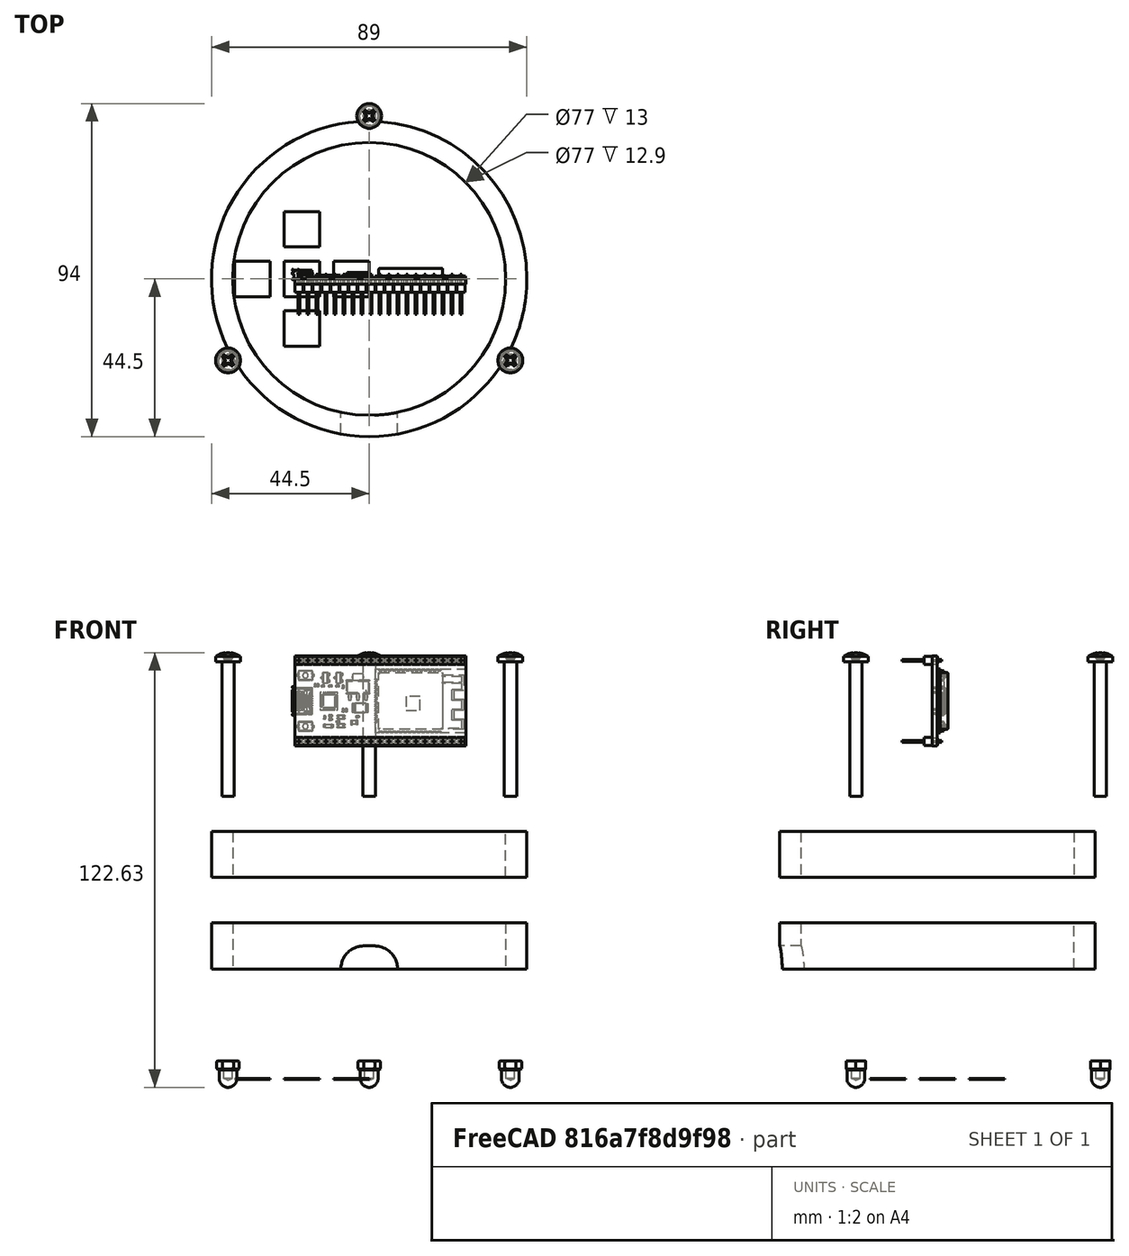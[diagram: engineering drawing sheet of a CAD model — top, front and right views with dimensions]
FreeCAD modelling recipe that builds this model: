
FCSTD DOCUMENT  (FreeCAD 2022.709R28846 (Git))
Label: infinity_02_exploded2
License: Other
LicenseURL: https://ohwr.org/project/cernohl/wikis/Documents/CERN-OHL-version-2
objects: Part::Feature×98, TechDraw::DrawViewDimension×36, TechDraw::DrawViewBalloon×17, PartDesign::ShapeBinder×12, TechDraw::DrawProjGroupItem×12, Sketcher::SketchObject×10, App::DocumentObjectGroupPython×9, PartDesign::Body×8, TechDraw::DrawSVGTemplate×8, TechDraw::DrawPage×8, TechDraw::DrawHatch×8, PartDesign::Plane×7, PartDesign::Pad×7, Part::FeaturePython×6, TechDraw::DrawProjGroup×6, Part::Part2DObjectPython×4, App::DocumentObjectGroup×3, PartDesign::Pocket×2, TechDraw::DrawViewPart×2, Spreadsheet::Sheet×1, +2 more types
note: 172 computed .brp shape members not serialized (recipe doc carries the construction recipe); baked Part::Feature solids carry a one-line shape summary decoded from their .brp

FEATURE [Spreadsheet::Sheet] Spreadsheet
  PythonMode = false
  ShowCells = 0
  TreeRank = 0
  cells = B1=Enter board size values here manually; C1=NOTES; D1=Micro_Pro; E1=Nano; F1=ESP8266 NodeMCU; G1=ESP32 NodeMCU; H1=Add more boards; I1=Add more boards; A2=Length of the microcontroller board - choose from list (and add more as required); B2(Length)==48mm; D2==34mm; E2==47mm; F2==48mm; G2==48mm; A3=Width of the microcontroller board; B3(width)==26mm; D3==21mm; E3==21mm; F3==26mm; G3==26mm; A4=Screw hole diameter; B4(screw_hole_dia)==3mm; C4=Adds 0.2mm to screw hole diameter; A5=Main Inner circumference; B5(inner_circumference)==240mm; C5=for ESP32 IoT course, make this number divisible by 12 so that 12 LEDs can be placed around circumference for a future clock; A6=Acrylic Thickness; B6(acrylic_thickness)==2.9mm; A7=LED strip width; B7(led_strip_width)==10mm; C7=use this to adjust the height of the upper spacer
FEATURE [Sketcher::SketchObject] Sketch005
  ArcFitTolerance = 0
  AttachmentSupport = -> [XY_Plane010]
  FullyConstrained = true
  MapMode = 5
  Support = -> [XY_Plane010]
  TreeRank = 0
  expr: Constraints[1] = Spreadsheet.inner_circumference / 3.14159
  sketch-geometry (53):
    g0: Circle CenterX=0 CenterY=0 CenterZ=0 NormalX=0 NormalY=0 NormalZ=1 AngleXU=0 Radius=38.1972
    g1: Circle CenterX=0 CenterY=0 CenterZ=0 NormalX=0 NormalY=0 NormalZ=1 AngleXU=0 Radius=44.5
    g2: Circle CenterX=0 CenterY=0 CenterZ=0 NormalX=0 NormalY=0 NormalZ=1 AngleXU=0 Radius=50
    g3: Circle CenterX=0 CenterY=0 CenterZ=0 NormalX=0 NormalY=0 NormalZ=1 AngleXU=0 Radius=38.5
    g4: LineSegment StartX=38.2587 StartY=9.99981 StartZ=0 EndX=28.1331 EndY=27.7894 EndZ=0
    g5: LineSegment StartX=28.1331 StartY=27.7894 StartZ=0 EndX=10.4692 EndY=38.1329 EndZ=0
    g6: LineSegment StartX=10.4692 StartY=38.1329 StartZ=0 EndX=-9.99981 EndY=38.2587 EndZ=0
    g7: LineSegment StartX=-9.99981 StartY=38.2587 StartZ=0 EndX=-27.7894 EndY=28.1331 EndZ=0
    g8: LineSegment StartX=-27.7894 StartY=28.1331 StartZ=0 EndX=-38.1329 EndY=10.4692 EndZ=0
    g9: LineSegment StartX=-38.1329 StartY=10.4692 StartZ=0 EndX=-38.2587 EndY=-9.99981 EndZ=0
    g10: LineSegment StartX=-38.2587 StartY=-9.99981 StartZ=0 EndX=-28.1331 EndY=-27.7894 EndZ=0
    g11: LineSegment StartX=-28.1331 StartY=-27.7894 StartZ=0 EndX=-10.4692 EndY=-38.1329 EndZ=0
    g12: LineSegment StartX=-10.4692 StartY=-38.1329 StartZ=0 EndX=9.99981 EndY=-38.2587 EndZ=0
    g13: LineSegment StartX=9.99981 StartY=-38.2587 StartZ=0 EndX=27.7894 EndY=-28.1331 EndZ=0
    g14: LineSegment StartX=27.7894 StartY=-28.1331 StartZ=0 EndX=38.1329 EndY=-10.4692 EndZ=0
    g15: LineSegment StartX=38.1329 StartY=-10.4692 StartZ=0 EndX=38.2587 EndY=9.99981 EndZ=0
    g16: Circle [constr] CenterX=0 CenterY=0 CenterZ=0 NormalX=0 NormalY=0 NormalZ=1 AngleXU=0 Radius=39.5439
    g17: LineSegment StartX=0 StartY=0 StartZ=0 EndX=0 EndY=38.1972 EndZ=0
    g18: LineSegment StartX=0 StartY=0 StartZ=0 EndX=19.0986 EndY=33.0798 EndZ=0
    g19: LineSegment StartX=0 StartY=0 StartZ=0 EndX=33.0798 EndY=19.0986 EndZ=0
    g20: LineSegment StartX=0 StartY=0 StartZ=0 EndX=38.1972 EndY=3.5e-15 EndZ=0
    g21: LineSegment StartX=0 StartY=0 StartZ=0 EndX=33.0798 EndY=-19.0986 EndZ=0
    g22: LineSegment StartX=0 StartY=0 StartZ=0 EndX=19.0986 EndY=-33.0798 EndZ=0
    g23: LineSegment StartX=0 StartY=0 StartZ=0 EndX=1.85e-14 EndY=-38.1972 EndZ=0
    g24: LineSegment StartX=0 StartY=0 StartZ=0 EndX=-19.0986 EndY=-33.0798 EndZ=0
    g25: LineSegment StartX=0 StartY=0 StartZ=0 EndX=-33.0798 EndY=-19.0986 EndZ=0
    g26: LineSegment StartX=0 StartY=0 StartZ=0 EndX=-38.1972 EndY=-5.03e-14 EndZ=0
    g27: LineSegment StartX=0 StartY=0 StartZ=0 EndX=-33.0798 EndY=19.0986 EndZ=0
    g28: LineSegment StartX=0 StartY=0 StartZ=0 EndX=-19.0986 EndY=33.0798 EndZ=0
    g29: LineSegment StartX=0 StartY=0 StartZ=0 EndX=3.99992 EndY=38.1726 EndZ=0
    g30: LineSegment StartX=0 StartY=0 StartZ=0 EndX=-3.99992 EndY=38.2218 EndZ=0
    g31: LineSegment StartX=0 StartY=0 StartZ=0 EndX=15.6469 EndY=35.101 EndZ=0
    g32: LineSegment StartX=0 StartY=0 StartZ=0 EndX=22.5504 EndY=31.0585 EndZ=0
    g33: LineSegment StartX=0 StartY=0 StartZ=0 EndX=31.1011 EndY=22.5749 EndZ=0
    g34: LineSegment StartX=0 StartY=0 StartZ=0 EndX=35.0584 EndY=15.6223 EndZ=0
    g35: LineSegment StartX=0 StartY=0 StartZ=0 EndX=38.2218 EndY=3.99992 EndZ=0
    g36: LineSegment StartX=0 StartY=0 StartZ=0 EndX=38.1726 EndY=-3.99992 EndZ=0
    g37: LineSegment StartX=0 StartY=0 StartZ=0 EndX=35.101 EndY=-15.6469 EndZ=0
    g38: LineSegment StartX=0 StartY=0 StartZ=0 EndX=31.0585 EndY=-22.5504 EndZ=0
    g39: LineSegment StartX=0 StartY=0 StartZ=0 EndX=22.5749 EndY=-31.1011 EndZ=0
    g40: LineSegment StartX=0 StartY=0 StartZ=0 EndX=15.6223 EndY=-35.0584 EndZ=0
    g41: LineSegment StartX=0 StartY=0 StartZ=0 EndX=3.99992 EndY=-38.2218 EndZ=0
    g42: LineSegment StartX=0 StartY=0 StartZ=0 EndX=-3.99992 EndY=-38.1726 EndZ=0
    g43: LineSegment StartX=0 StartY=0 StartZ=0 EndX=-15.6469 EndY=-35.101 EndZ=0
    g44: LineSegment StartX=0 StartY=0 StartZ=0 EndX=-22.5504 EndY=-31.0585 EndZ=0
    g45: LineSegment StartX=0 StartY=0 StartZ=0 EndX=-31.1011 EndY=-22.5749 EndZ=0
    g46: LineSegment StartX=0 StartY=0 StartZ=0 EndX=-35.0584 EndY=-15.6223 EndZ=0
    g47: LineSegment StartX=0 StartY=0 StartZ=0 EndX=-38.2218 EndY=-3.99992 EndZ=0
    g48: LineSegment StartX=0 StartY=0 StartZ=0 EndX=-38.1726 EndY=3.99992 EndZ=0
    g49: LineSegment StartX=0 StartY=0 StartZ=0 EndX=-35.101 EndY=15.6469 EndZ=0
    g50: LineSegment StartX=0 StartY=0 StartZ=0 EndX=-31.0585 EndY=22.5504 EndZ=0
    g51: LineSegment StartX=0 StartY=0 StartZ=0 EndX=-22.5749 EndY=31.1011 EndZ=0
    g52: LineSegment StartX=0 StartY=0 StartZ=0 EndX=-15.6223 EndY=35.0584 EndZ=0
  constraints (143):
    c: Coincident(g0,g-1)
    c: Diameter(g0) = 76.3944
    c: Coincident(g1,g0)
    c: Diameter(g1) = 89
    c: Coincident(g2,g0)
    c: Diameter(g2) = 100
    c: Coincident(g3,g0)
    c: Diameter(g3) = 77
    c: Coincident(g4,g5)
    c: Coincident(g5,g6)
    c: Coincident(g6,g7)
    c: Coincident(g7,g8)
    c: Coincident(g8,g9)
    c: Coincident(g9,g10)
    c: Coincident(g10,g11)
    c: Coincident(g11,g12)
    c: Coincident(g12,g13)
    c: Coincident(g13,g14)
    c: Coincident(g14,g15)
    c: Coincident(g15,g4)
    c: Equal(g4, g5-g15) x11
    c: PointOnObject(g4,g16)
    c: PointOnObject(g5,g16)
    c: PointOnObject(g6,g16)
    c: PointOnObject(g7,g16)
    c: PointOnObject(g8,g16)
    c: PointOnObject(g9,g16)
    c: PointOnObject(g10,g16)
    c: PointOnObject(g11,g16)
    c: PointOnObject(g12,g16)
    c: PointOnObject(g13,g16)
    c: PointOnObject(g14,g16)
    c: Coincident(g16,g0)
    c: Coincident(g17,g0)
    c: PointOnObject(g17,g6)
    c: Distance(g17,g6) = 10
    c: Coincident(g18,g0)
    c: PointOnObject(g18,g5)
    c: Coincident(g19,g0)
    c: PointOnObject(g19,g4)
    c: Coincident(g20,g0)
    c: PointOnObject(g20,g15)
    c: Coincident(g21,g0)
    c: PointOnObject(g21,g14)
    c: Coincident(g22,g0)
    c: PointOnObject(g22,g13)
    c: Coincident(g23,g0)
    c: PointOnObject(g23,g12)
    c: Coincident(g24,g0)
    c: PointOnObject(g24,g11)
    c: Coincident(g25,g0)
    c: PointOnObject(g25,g10)
    c: Coincident(g26,g0)
    c: PointOnObject(g26,g9)
    c: Coincident(g27,g0)
    c: PointOnObject(g27,g8)
    c: Coincident(g28,g0)
    c: PointOnObject(g28,g7)
    c: Angle(g18,g17) = 0.523599
    c: Angle(g19,g18) = 0.523599
    c: Angle(g20,g19) = 0.523599
    c: Angle(g21,g20) = 0.523599
    c: Angle(g22,g21) = 0.523599
    c: Angle(g23,g22) = 0.523599
    c: Angle(g24,g23) = 0.523599
    c: Angle(g25,g24) = 0.523599
    c: Angle(g26,g25) = 0.523599
    c: Angle(g27,g26) = 0.523599
    c: Angle(g28,g27) = 0.523599
    c: PointOnObject(g4,g16)
    c: Vertical(g17)
    c: PointOnObject(g17,g0)
    c: Coincident(g29,g0)
    c: PointOnObject(g29,g6)
    c: Coincident(g30,g0)
    c: Symmetric(g30,g29,g17)
    c: Distance(g29,g30) = 8
    c: Coincident(g31,g0)
    c: PointOnObject(g31,g5)
    c: Coincident(g32,g0)
    c: PointOnObject(g32,g5)
    c: Angle(g31,g30) = 0.523599
    c: Angle(g32,g29) = 0.523599
    c: Coincident(g33,g0)
    c: PointOnObject(g33,g4)
    c: Coincident(g34,g0)
    c: PointOnObject(g34,g4)
    c: Angle(g33,g31) = 0.523599
    c: Angle(g34,g32) = 0.523599
    c: Coincident(g35,g0)
    c: PointOnObject(g35,g15)
    c: Coincident(g36,g0)
    c: PointOnObject(g36,g15)
    c: Angle(g35,g33) = 0.523599
    c: Angle(g36,g34) = 0.523599
    c: Coincident(g37,g0)
    c: PointOnObject(g37,g14)
    c: Coincident(g38,g0)
    c: PointOnObject(g38,g14)
    c: Angle(g37,g35) = 0.523599
    c: Angle(g38,g36) = 0.523599
    c: Coincident(g39,g0)
    c: PointOnObject(g39,g13)
    c: Coincident(g40,g0)
    c: PointOnObject(g40,g13)
    c: Angle(g39,g37) = 0.523599
    c: Angle(g40,g38) = 0.523599
    c: Coincident(g41,g0)
    c: PointOnObject(g41,g12)
    c: Coincident(g42,g0)
    c: PointOnObject(g42,g12)
    c: Angle(g41,g39) = 0.523599
    c: Angle(g42,g40) = 0.523599
    c: Coincident(g43,g0)
    c: PointOnObject(g43,g11)
    c: Coincident(g44,g0)
    c: PointOnObject(g44,g11)
    c: Angle(g43,g41) = 0.523599
    c: Angle(g44,g42) = 0.523599
    c: Coincident(g45,g0)
    c: PointOnObject(g45,g10)
    c: Coincident(g46,g0)
    c: PointOnObject(g46,g10)
    c: Angle(g45,g43) = 0.523599
    c: Angle(g46,g44) = 0.523599
    c: Coincident(g47,g0)
    c: PointOnObject(g47,g9)
    c: Coincident(g48,g0)
    c: PointOnObject(g48,g9)
    c: Angle(g47,g45) = 0.523599
    c: Angle(g48,g46) = 0.523599
    c: Coincident(g49,g0)
    c: PointOnObject(g49,g8)
    c: Coincident(g50,g0)
    c: PointOnObject(g50,g8)
    c: Angle(g49,g47) = 0.523599
    c: Angle(g50,g48) = 0.523599
    c: Coincident(g51,g0)
    c: PointOnObject(g51,g7)
    c: Coincident(g52,g0)
    c: PointOnObject(g52,g7)
    c: Angle(g51,g49) = 0.523599
    c: Angle(g52,g50) = 0.523599
FEATURE [PartDesign::Body] Body010
  AutoGroupSolids = false
  ClaimAllChildren = false
  ExportMode = 0
  Group = -> [Sketch005]
  Origin = -> Origin013
  TreeRank = 0
  _ExportChildren = -> [Sketch005]
  _GroupVersion = 1
FEATURE [PartDesign::ShapeBinder] ShapeBinder
  Support = -> [Sketch005]
  TraceSupport = false
  TreeRank = 0
FEATURE [PartDesign::Plane] DatumPlane
  AttachmentSupport = -> [ShapeBinder]
  Length = 10
  MapMode = 11
  MinimumLength = 10
  MinimumWidth = 10
  Placement = pos=(0,0,0) rot=(0,0,1;1.5708rad)
  ResizeMode = 0
  Support = -> [ShapeBinder]
  TreeRank = 0
  Width = 10
FEATURE [Sketcher::SketchObject] Sketch
  ArcFitTolerance = 0
  AttachmentSupport = -> [DatumPlane]
  ExternalGeometry = -> [ShapeBinder]
  FullyConstrained = true
  MapMode = 5
  Placement = pos=(0,0,0) rot=(0,0,1;1.5708rad)
  Support = -> [DatumPlane]
  TreeRank = 0
  sketch-geometry (2):
    g0: Circle CenterX=0 CenterY=0 CenterZ=0 NormalX=0 NormalY=0 NormalZ=1 AngleXU=0 Radius=44.5
    g1: Circle CenterX=0 CenterY=0 CenterZ=0 NormalX=0 NormalY=0 NormalZ=1 AngleXU=0 Radius=38.5
  constraints (4):
    c: Coincident(g0,g-4)
    c: Coincident(g1,g0)
    c: Equal(g1,g-4)
    c: Equal(g-3,g0)
FEATURE [PartDesign::Pad] Pad
  ClaimChildren = false
  Direction = (1,1,1)
  Fit = 0
  FitJoin = 0
  InnerFit = 0
  InnerFitJoin = 0
  InnerTaperAngle = 0
  InnerTaperAngleRev = 0
  Length = 5
  Length2 = 8
  NewSolid = false
  Placement = pos=(0,0,0) rot=(0,0,1;1.5708rad)
  Profile = -> Sketch
  Reversed = true
  Suppress = false
  TreeRank = 0
  Type = 4
  _ProfileBasedVersion = 0
FEATURE [PartDesign::Plane] DatumPlane002
  AttachmentOffset = pos=(0,0,0) rot=(1,0,0;1.5708rad)
  AttachmentSupport = -> [Pad]
  Length = 89
  MapMode = 45
  MinimumLength = 10
  MinimumWidth = 10
  Placement = pos=(3e-16,-1.42e-14,-1.5) rot=(1,0,0;1.5708rad)
  ResizeMode = 0
  Support = -> [Pad]
  TreeRank = 0
  Width = 13
FEATURE [Sketcher::SketchObject] Sketch007
  ArcFitTolerance = 0
  AttachmentSupport = -> [DatumPlane002]
  ExternalGeometry = -> [Pad]
  FullyConstrained = true
  MapMode = 5
  Placement = pos=(3e-16,-1.42e-14,-1.5) rot=(1,0,0;1.5708rad)
  Support = -> [DatumPlane002]
  TreeRank = 0
  sketch-geometry (4):
    g0: ArcOfCircle CenterX=-1.5 CenterY=-6.5 CenterZ=0 NormalX=0 NormalY=0 NormalZ=1 AngleXU=0 Radius=6.5 StartAngle=1.5708 EndAngle=4.71239
    g1: ArcOfCircle CenterX=1.5 CenterY=-6.5 CenterZ=0 NormalX=0 NormalY=0 NormalZ=1 AngleXU=0 Radius=6.5 StartAngle=4.71239 EndAngle=7.85398
    g2: LineSegment StartX=-1.5 StartY=-13 StartZ=0 EndX=1.5 EndY=-13 EndZ=0
    g3: LineSegment StartX=-1.5 StartY=9e-16 StartZ=0 EndX=1.5 EndY=1.8e-15 EndZ=0
  constraints (9):
    c: Tangent(g0,g3) = 1.5708
    c: Tangent(g0,g2) = -1.5708
    c: Tangent(g2,g1) = -1.5708
    c: Tangent(g3,g1) = 1.5708
    c: Horizontal(g2)
    c: DistanceX(g0,g1) = 3
    c: Symmetric(g1,g0,g-2)
    c: Radius(g0) = 6.5
    c: PointOnObject(g0,g-3)
FEATURE [PartDesign::Pocket] Pocket
  BaseFeature = -> Pad
  ClaimChildren = false
  Fit = 0
  FitJoin = 0
  InnerFit = 0
  InnerFitJoin = 0
  InnerTaperAngle = 0
  InnerTaperAngleRev = 0
  Length = 26
  Length2 = 100
  NewSolid = false
  Placement = pos=(0,0,0) rot=(0,0,1;1.5708rad)
  Profile = -> Sketch007
  Reversed = true
  Suppress = false
  TreeRank = 0
  Type = 1
  _ProfileBasedVersion = 0
FEATURE [PartDesign::Body] Body  label="PCB_lower_spacer"
  AutoGroupSolids = false
  ClaimAllChildren = false
  ExportMode = 0
  Group = -> [ShapeBinder,DatumPlane,Sketch,Pad,DatumPlane002,Sketch007,Pocket]
  Origin = -> Origin
  Placement = pos=(0,0,-67) rot=(0,0,1;0rad)
  Tip = -> Pocket
  TreeRank = 0
  _ExportChildren = -> [ShapeBinder,DatumPlane,Pad,DatumPlane002,Pocket]
  _GroupVersion = 1
FEATURE [PartDesign::ShapeBinder] ShapeBinder002
  Support = -> [Sketch005]
  TraceSupport = false
  TreeRank = 0
FEATURE [PartDesign::ShapeBinder] ShapeBinder003
  Placement = pos=(0,0,-67) rot=(0,0,1;0rad)
  Support = -> [Body]
  TraceSupport = false
  TreeRank = 0
FEATURE [PartDesign::Plane] DatumPlane004
  AttachmentSupport = -> [ShapeBinder003]
  Length = 100
  MapMode = 5
  MinimumLength = 10
  MinimumWidth = 10
  Placement = pos=(0,0,-62) rot=(0,0,1;0rad)
  ResizeMode = 0
  Support = -> [ShapeBinder003]
  TreeRank = 0
  Width = 99.9333
FEATURE [Sketcher::SketchObject] Sketch009
  ArcFitTolerance = 0
  AttachmentSupport = -> [DatumPlane004]
  ExternalGeometry = -> [ShapeBinder002]
  FullyConstrained = true
  MapMode = 5
  Placement = pos=(0,0,-62) rot=(0,0,1;0rad)
  Support = -> [DatumPlane004]
  TreeRank = 0
  expr: Constraints[1] = Spreadsheet.screw_hole_dia
  sketch-geometry (8):
    g0: Circle CenterX=0 CenterY=0 CenterZ=0 NormalX=0 NormalY=0 NormalZ=1 AngleXU=0 Radius=50
    g1: Circle CenterX=0 CenterY=46 CenterZ=0 NormalX=0 NormalY=0 NormalZ=1 AngleXU=0 Radius=1.5
    g2: Circle CenterX=-39.8372 CenterY=-23 CenterZ=0 NormalX=0 NormalY=0 NormalZ=1 AngleXU=0 Radius=1.5
    g3: Circle CenterX=39.8372 CenterY=-23 CenterZ=0 NormalX=0 NormalY=0 NormalZ=1 AngleXU=0 Radius=1.5
    g4: LineSegment [constr] StartX=0 StartY=46 StartZ=0 EndX=-39.8372 EndY=-23 EndZ=0
    g5: LineSegment [constr] StartX=-39.8372 StartY=-23 StartZ=0 EndX=39.8372 EndY=-23 EndZ=0
    g6: LineSegment [constr] StartX=39.8372 StartY=-23 StartZ=0 EndX=0 EndY=46 EndZ=0
    g7: Circle [constr] CenterX=0 CenterY=0 CenterZ=0 NormalX=0 NormalY=0 NormalZ=1 AngleXU=0 Radius=46
  constraints (19):
    c: Equal(g-3,g0)
    c: Diameter(g1) = 3
    c: Equal(g1,g2)
    c: Equal(g1,g3)
    c: PointOnObject(g1,g-2)
    c: Tangent(g1,g-5)
    c: Tangent(g2,g-5)
    c: Tangent(g3,g-5)
    c: Coincident(g4,g5)
    c: Coincident(g5,g6)
    c: Coincident(g6,g4)
    c: Equal(g4,g5)
    c: Equal(g4,g6)
    c: PointOnObject(g4,g7)
    c: Coincident(g6,g1)
    c: Coincident(g2,g4)
    c: Coincident(g3,g5)
    c: Coincident(g0,g-5)
    c: Coincident(g7,g0)
FEATURE [PartDesign::Pad] Pad002
  ClaimChildren = false
  Direction = (1,1,1)
  Fit = 0
  FitJoin = 0
  InnerFit = 0
  InnerFitJoin = 0
  InnerTaperAngle = 0
  InnerTaperAngleRev = 0
  Length = 2.9
  Length2 = 100
  NewSolid = false
  Placement = pos=(0,0,-62) rot=(0,0,1;0rad)
  Profile = -> Sketch009
  Suppress = false
  TreeRank = 0
  Type = 0
  _ProfileBasedVersion = 0
  expr: Length = Spreadsheet.acrylic_thickness
FEATURE [Part::Feature] Solid089
  TreeRank = 0
  shape: bbox 0.66 x 0.051 x 0.304 mm, 6 faces (baked)
FEATURE [Part::Feature] Solid090
  TreeRank = 0
  shape: bbox 0.5016 x 0.5016 x 1 mm, 66 faces (baked)
FEATURE [Part::Feature] Solid091
  TreeRank = 0
  shape: bbox 0.66 x 0.051 x 0.304 mm, 6 faces (baked)
FEATURE [Part::Feature] Solid092
  TreeRank = 0
  shape: bbox 0.66 x 0.051 x 0.304 mm, 6 faces (baked)
FEATURE [Part::Feature] Solid093
  TreeRank = 0
  shape: bbox 1.02 x 0.52 x 0.52 mm, 15 faces (baked)
FEATURE [Part::Feature] Solid094
  TreeRank = 0
  shape: bbox 0.65 x 1.325 x 2.3 mm, 11 faces (baked)
FEATURE [Part::Feature] Solid095
  TreeRank = 0
  shape: bbox 2.126 x 0.2178 x 1.073 mm, 52 faces (baked)
FEATURE [Part::Feature] Solid096
  TreeRank = 0
  shape: bbox 0.4 x 0.2 x 0.8 mm, 8 faces (baked)
FEATURE [Part::Feature] Solid097
  TreeRank = 0
  shape: bbox 4.2 x 1.55 x 0.3 mm, 15 faces (baked)
FEATURE [Part::Feature] Solid098
  TreeRank = 0
  shape: bbox 1.624 x 0.5 x 1.624 mm, 6 faces (baked)
FEATURE [Part::Feature] Solid099
  TreeRank = 0
  shape: bbox 1.02 x 0.52 x 0.52 mm, 15 faces (baked)
FEATURE [Part::Feature] Solid100
  TreeRank = 0
  shape: bbox 1 x 0.5016 x 0.5016 mm, 66 faces (baked)
FEATURE [Part::Feature] Solid101
  TreeRank = 0
  shape: bbox 3.9 x 1.7 x 2.5 mm, 6 faces (baked)
FEATURE [Part::Feature] Solid102
  TreeRank = 0
  shape: bbox 0.4 x 0.2 x 0.8 mm, 8 faces (baked)
FEATURE [Part::Feature] Solid103
  TreeRank = 0
  shape: bbox 4.2 x 1.55 x 0.3 mm, 15 faces (baked)
FEATURE [Part::Feature] Solid104
  TreeRank = 0
  shape: bbox 4.2 x 1.55 x 0.3 mm, 15 faces (baked)
FEATURE [Part::Feature] Solid105
  TreeRank = 0
  shape: bbox 1 x 0.5016 x 0.5016 mm, 66 faces (baked)
FEATURE [Part::Feature] Solid106
  TreeRank = 0
  shape: bbox 6.707 x 1.804 x 3.709 mm, 14 faces (baked)
FEATURE [Part::Feature] Solid107
  TreeRank = 0
  shape: bbox 0.52 x 0.52 x 1.02 mm, 15 faces (baked)
FEATURE [Part::Feature] Solid108
  TreeRank = 0
  shape: bbox 2 x 0.8516 x 1.252 mm, 66 faces (baked)
FEATURE [Part::Feature] Solid109
  TreeRank = 0
  shape: bbox 1.624 x 0.5 x 1.624 mm, 6 faces (baked)
FEATURE [Part::Feature] Solid110
  TreeRank = 0
  shape: bbox 3.9 x 1.2 x 0.1 mm, 14 faces (baked)
FEATURE [Part::Feature] Solid111
  TreeRank = 0
  shape: bbox 0.8392 x 0.9032 x 1.792 mm, 14 faces (baked)
FEATURE [Part::Feature] Solid112
  TreeRank = 0
  shape: bbox 3.9 x 1.7 x 2.5 mm, 6 faces (baked)
FEATURE [Part::Feature] Solid113
  TreeRank = 0
  shape: bbox 2.5 x 1.11 x 3 mm, 49 faces (baked)
FEATURE [Part::Feature] Solid114
  TreeRank = 0
  shape: bbox 0.304 x 0.051 x 0.66 mm, 6 faces (baked)
FEATURE [Part::Feature] Solid115
  TreeRank = 0
  shape: bbox 1.333 x 0.3705 x 1.073 mm, 18 faces (baked)
FEATURE [Part::Feature] Solid116 .. Solid121  x6 (patterned run collapsed; names and placements below)
  TreeRank = 0
  shape: bbox 0.304 x 0.051 x 0.66 mm, 6 faces (baked)
FEATURE [Part::Feature] Solid122
  TreeRank = 0
  shape: bbox 0.66 x 0.051 x 0.304 mm, 6 faces (baked)
FEATURE [Part::Feature] Solid123
  TreeRank = 0
  shape: bbox 0.52 x 0.52 x 1.02 mm, 15 faces (baked)
FEATURE [Part::Feature] Solid124
  TreeRank = 0
  shape: bbox 0.66 x 0.051 x 0.304 mm, 6 faces (baked)
FEATURE [Part::Feature] Solid125
  TreeRank = 0
  shape: bbox 3.9 x 1.2 x 0.1 mm, 14 faces (baked)
FEATURE [Part::Feature] Solid126 .. Solid130  x5 (patterned run collapsed; names and placements below)
  TreeRank = 0
  shape: bbox 0.66 x 0.051 x 0.304 mm, 6 faces (baked)
FEATURE [Part::Feature] Solid131
  TreeRank = 0
  shape: bbox 4.16 x 2.41 x 6.91 mm, 176 faces (baked)
FEATURE [Part::Feature] Solid132
  TreeRank = 0
  shape: bbox 0.304 x 0.051 x 0.66 mm, 6 faces (baked)
FEATURE [Part::Feature] Solid133
  TreeRank = 0
  shape: bbox 0.4 x 0.2 x 0.8 mm, 8 faces (baked)
FEATURE [Part::Feature] Solid134 .. Solid138  x5 (patterned run collapsed; names and placements below)
  TreeRank = 0
  shape: bbox 0.304 x 0.051 x 0.66 mm, 6 faces (baked)
FEATURE [Part::Feature] Solid139
  TreeRank = 0
  shape: bbox 0.52 x 0.52 x 1.02 mm, 15 faces (baked)
FEATURE [Part::Feature] Solid140
  TreeRank = 0
  shape: bbox 0.304 x 0.051 x 0.66 mm, 6 faces (baked)
FEATURE [Part::Feature] Solid141
  TreeRank = 0
  shape: bbox 3.352 x 0.051 x 3.352 mm, 6 faces (baked)
FEATURE [Part::Feature] Solid142
  TreeRank = 0
  shape: bbox 1.65 x 1.05 x 1.05 mm, 14 faces (baked)
FEATURE [Part::Feature] Solid143
  TreeRank = 0
  shape: bbox 0.4875 x 0.5625 x 0.9375 mm, 11 faces (baked)
FEATURE [Part::Feature] Solid144
  TreeRank = 0
  shape: bbox 0.4 x 0.2 x 0.8 mm, 8 faces (baked)
FEATURE [Part::Feature] Solid145
  TreeRank = 0
  shape: bbox 1.333 x 0.3705 x 1.073 mm, 18 faces (baked)
FEATURE [Part::Feature] Solid146
  TreeRank = 0
  shape: bbox 0.4875 x 0.5625 x 0.9375 mm, 11 faces (baked)
FEATURE [Part::Feature] Solid147
  TreeRank = 0
  shape: bbox 1 x 0.5016 x 0.5016 mm, 66 faces (baked)
FEATURE [Part::Feature] Solid148
  TreeRank = 0
  shape: bbox 0.8392 x 0.9032 x 1.792 mm, 14 faces (baked)
FEATURE [Part::Feature] Solid149
  TreeRank = 0
  shape: bbox 1.02 x 0.52 x 0.52 mm, 15 faces (baked)
FEATURE [Part::Feature] Solid150
  TreeRank = 0
  shape: bbox 3.151 x 0.9032 x 1.792 mm, 14 faces (baked)
FEATURE [Part::Feature] Solid151
  TreeRank = 0
  shape: bbox 3.3 x 1.775 x 2.7 mm, 7 faces (baked)
FEATURE [Part::Feature] Solid152
  TreeRank = 0
  shape: bbox 0.65 x 1.325 x 2.3 mm, 11 faces (baked)
FEATURE [Part::Feature] Solid153
  TreeRank = 0
  shape: bbox 48.28 x 11.27 x 25.42 mm, 1344 faces (baked)
FEATURE [Part::Feature] Solid154
  TreeRank = 0
  shape: bbox 0.1854 x 0.003 x 0.1854 mm, 4 faces (baked)
FEATURE [Part::Feature] Solid155
  TreeRank = 0
  shape: bbox 2.126 x 0.2178 x 1.073 mm, 52 faces (baked)
FEATURE [Part::Feature] Solid156
  TreeRank = 0
  shape: bbox 4.2 x 1.55 x 0.3 mm, 15 faces (baked)
FEATURE [Part::Feature] Solid157
  TreeRank = 0
  shape: bbox 3.9 x 0.1 x 2.5 mm, 30 faces (baked)
FEATURE [Part::Feature] Solid158
  TreeRank = 0
  shape: bbox 0.52 x 0.52 x 1.02 mm, 15 faces (baked)
FEATURE [Part::Feature] Solid159
  TreeRank = 0
  shape: bbox 0.1 x 0.6 x 0.8 mm, 6 faces (baked)
FEATURE [Part::Feature] Solid160
  TreeRank = 0
  shape: bbox 2.5 x 1.11 x 3 mm, 49 faces (baked)
FEATURE [Part::Feature] Solid161
  TreeRank = 0
  shape: bbox 0.1 x 0.6 x 0.8 mm, 6 faces (baked)
FEATURE [Part::Feature] Solid162
  TreeRank = 0
  shape: bbox 3.9 x 1.2 x 0.1 mm, 14 faces (baked)
FEATURE [Part::Feature] Solid163
  TreeRank = 0
  shape: bbox 1.02 x 0.52 x 0.52 mm, 15 faces (baked)
FEATURE [Part::Feature] Solid164
  TreeRank = 0
  shape: bbox 5.63 x 3.797 x 8.183 mm, 257 faces (baked)
FEATURE [Part::Feature] Solid165
  TreeRank = 0
  shape: bbox 3.9 x 0.1 x 2.5 mm, 30 faces (baked)
FEATURE [Part::Feature] Solid166
  TreeRank = 0
  shape: bbox 4.2 x 1.55 x 0.3 mm, 15 faces (baked)
FEATURE [Part::Feature] Solid167
  TreeRank = 0
  shape: bbox 0.1 x 0.6 x 0.8 mm, 6 faces (baked)
FEATURE [Part::Feature] Solid168
  TreeRank = 0
  shape: bbox 0.1 x 0.6 x 0.8 mm, 6 faces (baked)
FEATURE [Part::Feature] Solid169
  TreeRank = 0
  shape: bbox 3.9 x 1.2 x 0.1 mm, 14 faces (baked)
FEATURE [Part::Feature] Solid170
  TreeRank = 0
  shape: bbox 0.52 x 0.52 x 1.02 mm, 15 faces (baked)
FEATURE [Part::Feature] Solid171
  TreeRank = 0
  shape: bbox 0.8392 x 0.9032 x 1.792 mm, 14 faces (baked)
FEATURE [Part::Feature] Solid172
  TreeRank = 0
  shape: bbox 0.2502 x 0.002 x 0.2502 mm, 4 faces (baked)
FEATURE [Part::Feature] Solid173
  TreeRank = 0
  shape: bbox 5.004 x 0.94 x 5.004 mm, 6 faces (baked)
FEATURE [Part::Feature] Solid174
  TreeRank = 0
  shape: bbox 0.66 x 0.051 x 0.304 mm, 6 faces (baked)
FEATURE [Part::Feature] Solid175
  TreeRank = 0
  shape: bbox 25.54 x 3.035 x 18.07 mm, 584 faces (baked)
FEATURE [Part::Feature] Solid176
  TreeRank = 0
  shape: bbox 0.66 x 0.051 x 0.304 mm, 6 faces (baked)
FEATURE [Part::Feature] Solid177
  TreeRank = 0
  shape: bbox 0.66 x 0.051 x 0.304 mm, 6 faces (baked)
FEATURE [Part::Feature] Solid178
  TreeRank = 0
  shape: bbox 0.66 x 0.051 x 0.304 mm, 6 faces (baked)
FEATURE [Part::Compound2] Compound001  label="ESP32Wroom4"
  Links = -> [Solid089,Solid090,Solid091,Solid092,Solid093,Solid094,Solid095,Solid096,Solid097,Solid098,Solid099,Solid100,Solid101,Solid102,Solid103,Solid104,Solid105,Solid106,Solid107,Solid108,Solid109,Solid110,Solid111,Solid112,Solid113,Solid114,Solid115,Solid116,Solid117,Solid118,Solid119,Solid120,Solid121,Solid122,Solid123,Solid124,Solid125,Solid126,Solid127,Solid128,Solid129,Solid130,Solid131,Solid132,+46 more]
  Placement = pos=(0.5,-15,-90) rot=(-0.57735,-0.57735,0.57735;2.0944rad)
  TreeRank = 0
FEATURE [Sketcher::SketchObject] Sketch010
  ArcFitTolerance = 0
  AttachmentSupport = -> [Pad002]
  ExternalGeometry = -> [ShapeBinder002]
  FullyConstrained = true
  MapMode = 5
  Placement = pos=(0,0,-59.1) rot=(0,0,1;0rad)
  Support = -> [Pad002]
  TreeRank = 0
  sketch-geometry (5):
    g0: ArcOfCircle CenterX=-4 CenterY=-34.5 CenterZ=0 NormalX=0 NormalY=0 NormalZ=1 AngleXU=0 Radius=2 StartAngle=1.5708 EndAngle=4.71239
    g1: ArcOfCircle CenterX=4 CenterY=-34.5 CenterZ=0 NormalX=0 NormalY=0 NormalZ=1 AngleXU=0 Radius=2 StartAngle=4.71239 EndAngle=7.85398
    g2: LineSegment StartX=-4 StartY=-36.5 StartZ=0 EndX=4 EndY=-36.5 EndZ=0
    g3: LineSegment StartX=-4 StartY=-32.5 StartZ=0 EndX=4 EndY=-32.5 EndZ=0
    g4: LineSegment [constr] StartX=0 StartY=-38.5 StartZ=0 EndX=0 EndY=-36.5 EndZ=0
  constraints (13):
    c: Tangent(g0,g3) = 1.5708
    c: Tangent(g0,g2) = -1.5708
    c: Tangent(g2,g1) = -1.5708
    c: Tangent(g3,g1) = 1.5708
    c: Horizontal(g2)
    c: Diameter(g0) = 4
    c: Symmetric(g0,g1,g-2)
    c: DistanceX(g0,g1) = 8
    c: PointOnObject(g4,g-3)
    c: PointOnObject(g4,g2)
    c: Vertical(g4)
    c: PointOnObject(g4,g-2)
    c: DistanceY(g4,g4) = 2
FEATURE [PartDesign::Pocket] Pocket001
  BaseFeature = -> Pad002
  ClaimChildren = false
  Fit = 0
  FitJoin = 0
  InnerFit = 0
  InnerFitJoin = 0
  InnerTaperAngle = 0
  InnerTaperAngleRev = 0
  Length = 5
  Length2 = 100
  NewSolid = false
  Placement = pos=(0,0,-62) rot=(0,0,1;0rad)
  Profile = -> Sketch010
  Suppress = false
  TreeRank = 0
  Type = 1
  _ProfileBasedVersion = 0
FEATURE [PartDesign::Body] Body012  label="Mirror"
  AutoGroupSolids = false
  ClaimAllChildren = false
  ExportMode = 0
  Group = -> [ShapeBinder002,ShapeBinder003,DatumPlane004,Sketch009,Pad002,Sketch010,Pocket001]
  Origin = -> Origin015
  Placement = pos=(0,0,5) rot=(0,0,1;0rad)
  Tip = -> Pocket001
  TreeRank = 0
  _ExportChildren = -> [ShapeBinder002,ShapeBinder003,DatumPlane004,Pad002,Pocket001]
  _GroupVersion = 1
FEATURE [PartDesign::ShapeBinder] ShapeBinder004 .. ShapeBinder007  x4 (patterned run collapsed; names and placements below)
  Support = -> [Sketch005]
  TraceSupport = false
  TreeRank = 0
FEATURE [PartDesign::Plane] DatumPlane008
  AttachmentSupport = -> [Pocket]
  Length = 98.9466
  MapMode = 5
  MinimumLength = 10
  MinimumWidth = 10
  Placement = pos=(0,0,-8) rot=(0.707107,0.707107,0;3.14159rad)
  ResizeMode = 0
  Support = -> [Pocket]
  TreeRank = 0
  Width = 99.95
FEATURE [Sketcher::SketchObject] Sketch014
  ArcFitTolerance = 0
  AttachmentSupport = -> [DatumPlane008]
  ExternalGeometry = -> [ShapeBinder007]
  FullyConstrained = true
  MapMode = 5
  Placement = pos=(0,0,-8) rot=(0.707107,0.707107,0;3.14159rad)
  Support = -> [DatumPlane008]
  TreeRank = 0
  expr: Constraints[2] = Spreadsheet.screw_hole_dia
  sketch-geometry (62):
    g0: ArcOfCircle CenterX=-7e-16 CenterY=7e-16 CenterZ=0 NormalX=0 NormalY=0 NormalZ=1 AngleXU=0 Radius=50 StartAngle=3.35146 EndAngle=9.21491
    g1: Circle CenterX=-23 CenterY=-39.8372 CenterZ=0 NormalX=0 NormalY=0 NormalZ=1 AngleXU=0 Radius=1.5
    g2: Circle CenterX=46 CenterY=0 CenterZ=0 NormalX=0 NormalY=0 NormalZ=1 AngleXU=0 Radius=1.5
    g3: Circle CenterX=-23 CenterY=39.8372 CenterZ=0 NormalX=0 NormalY=0 NormalZ=1 AngleXU=0 Radius=1.5
    g4: LineSegment [constr] StartX=-23 StartY=-39.8372 StartZ=0 EndX=46 EndY=0 EndZ=0
    g5: LineSegment [constr] StartX=46 StartY=0 StartZ=0 EndX=-23 EndY=39.8372 EndZ=0
    g6: LineSegment [constr] StartX=-23 StartY=39.8372 StartZ=0 EndX=-23 EndY=-39.8372 EndZ=0
    g7: Circle [constr] CenterX=-7e-16 CenterY=7e-16 CenterZ=0 NormalX=0 NormalY=0 NormalZ=1 AngleXU=0 Radius=46
    g8: ArcOfCircle CenterX=22 CenterY=0 CenterZ=0 NormalX=0 NormalY=0 NormalZ=1 AngleXU=0 Radius=6 StartAngle=0.523599 EndAngle=5.75959
    g9: ArcOfCircle CenterX=34 CenterY=0 CenterZ=0 NormalX=0 NormalY=0 NormalZ=1 AngleXU=0 Radius=2 StartAngle=4.71239 EndAngle=7.85398
    g10: LineSegment StartX=28.9282 StartY=-2 StartZ=0 EndX=34 EndY=-2 EndZ=0
    g11: LineSegment StartX=28.9282 StartY=2 StartZ=0 EndX=34 EndY=2 EndZ=0
    g12: ArcOfCircle CenterX=28.9282 CenterY=4 CenterZ=0 NormalX=0 NormalY=0 NormalZ=1 AngleXU=0 Radius=2 StartAngle=3.66519 EndAngle=4.71239
    g13: ArcOfCircle CenterX=28.9282 CenterY=-4 CenterZ=0 NormalX=0 NormalY=0 NormalZ=1 AngleXU=0 Radius=2 StartAngle=1.5708 EndAngle=2.61799
    g14: LineSegment [constr] StartX=-5 StartY=7e-16 StartZ=0 EndX=5 EndY=7e-16 EndZ=0
    g15: LineSegment [constr] StartX=5 StartY=7e-16 StartZ=0 EndX=5 EndY=-10 EndZ=0
    g16: LineSegment [constr] StartX=5 StartY=-10 StartZ=0 EndX=-5 EndY=-10 EndZ=0
    g17: LineSegment [constr] StartX=-5 StartY=-10 StartZ=0 EndX=-5 EndY=0 EndZ=0
    g18: LineSegment [constr] StartX=-19 StartY=-14 StartZ=0 EndX=-9 EndY=-14 EndZ=0
    g19: LineSegment [constr] StartX=-9 StartY=-14 StartZ=0 EndX=-9 EndY=-24 EndZ=0
    g20: LineSegment [constr] StartX=-9 StartY=-24 StartZ=0 EndX=-19 EndY=-24 EndZ=0
    g21: LineSegment [constr] StartX=-19 StartY=-24 StartZ=0 EndX=-19 EndY=-14 EndZ=0
    g22: LineSegment [constr] StartX=9 StartY=-14 StartZ=0 EndX=19 EndY=-14 EndZ=0
    g23: LineSegment [constr] StartX=19 StartY=-14 StartZ=0 EndX=19 EndY=-24 EndZ=0
    g24: LineSegment [constr] StartX=19 StartY=-24 StartZ=0 EndX=9 EndY=-24 EndZ=0
    g25: LineSegment [constr] StartX=9 StartY=-24 StartZ=0 EndX=9 EndY=-14 EndZ=0
    g26: LineSegment [constr] StartX=-5 StartY=-14 StartZ=0 EndX=5 EndY=-14 EndZ=0
    g27: LineSegment [constr] StartX=5 StartY=-14 StartZ=0 EndX=5 EndY=-24 EndZ=0
    g28: LineSegment [constr] StartX=5 StartY=-24 StartZ=0 EndX=-5 EndY=-24 EndZ=0
    g29: LineSegment [constr] StartX=-5 StartY=-24 StartZ=0 EndX=-5 EndY=-14 EndZ=0
    g30: LineSegment [constr] StartX=-5 StartY=-28 StartZ=0 EndX=5 EndY=-28 EndZ=0
    g31: LineSegment [constr] StartX=5 StartY=-28 StartZ=0 EndX=5 EndY=-38 EndZ=0
    g32: LineSegment [constr] StartX=5 StartY=-38 StartZ=0 EndX=-5 EndY=-38 EndZ=0
    g33: LineSegment [constr] StartX=-5 StartY=-38 StartZ=0 EndX=-5 EndY=-28 EndZ=0
    g34: LineSegment [constr] StartX=-5 StartY=-10 StartZ=0 EndX=-5 EndY=-14 EndZ=0
    g35: LineSegment [constr] StartX=-5 StartY=-14 StartZ=0 EndX=-9 EndY=-14 EndZ=0
    g36: LineSegment [constr] StartX=5 StartY=-10 StartZ=0 EndX=5 EndY=-14 EndZ=0
    g37: LineSegment [constr] StartX=5 StartY=-14 StartZ=0 EndX=9 EndY=-14 EndZ=0
    g38: LineSegment [constr] StartX=5 StartY=-28 StartZ=0 EndX=5 EndY=-24 EndZ=0
    g39: LineSegment [constr] StartX=5 StartY=-24 StartZ=0 EndX=9 EndY=-24 EndZ=0
    g40: LineSegment [constr] StartX=-5 StartY=-28 StartZ=0 EndX=-5 EndY=-24 EndZ=0
    g41: LineSegment [constr] StartX=-5 StartY=-24 StartZ=0 EndX=-9 EndY=-24 EndZ=0
    g42: LineSegment [constr] StartX=-7 StartY=-12 StartZ=0 EndX=7 EndY=-12 EndZ=0
    g43: LineSegment [constr] StartX=7 StartY=-12 StartZ=0 EndX=7 EndY=-26 EndZ=0
    g44: LineSegment [constr] StartX=7 StartY=-26 StartZ=0 EndX=-7 EndY=-26 EndZ=0
    g45: LineSegment [constr] StartX=-7 StartY=-26 StartZ=0 EndX=-7 EndY=-12 EndZ=0
    g46: LineSegment [constr] StartX=-1.3e-15 StartY=-12 StartZ=0 EndX=-1.3e-15 EndY=-26 EndZ=0
    g47: LineSegment [constr] StartX=7 StartY=-19 StartZ=0 EndX=-7 EndY=-19 EndZ=0
    g48: Circle CenterX=-7 CenterY=-12 CenterZ=0 NormalX=0 NormalY=0 NormalZ=1 AngleXU=0 Radius=1.5
    g49: Circle CenterX=-1.3e-15 CenterY=-12 CenterZ=0 NormalX=0 NormalY=0 NormalZ=1 AngleXU=0 Radius=1.5
    g50: Circle CenterX=7 CenterY=-12 CenterZ=0 NormalX=0 NormalY=0 NormalZ=1 AngleXU=0 Radius=1.5
    g51: Circle CenterX=7 CenterY=-19 CenterZ=0 NormalX=0 NormalY=0 NormalZ=1 AngleXU=0 Radius=1.5
    g52: Circle CenterX=7 CenterY=-26 CenterZ=0 NormalX=0 NormalY=0 NormalZ=1 AngleXU=0 Radius=1.5
    g53: Circle CenterX=-1.3e-15 CenterY=-26 CenterZ=0 NormalX=0 NormalY=0 NormalZ=1 AngleXU=0 Radius=1.5
    g54: Circle CenterX=-7 CenterY=-26 CenterZ=0 NormalX=0 NormalY=0 NormalZ=1 AngleXU=0 Radius=1.5
    g55: Circle CenterX=-7 CenterY=-19 CenterZ=0 NormalX=0 NormalY=0 NormalZ=1 AngleXU=0 Radius=1.5
    g56: ArcOfCircle CenterX=-36.9468 CenterY=1e-16 CenterZ=0 NormalX=0 NormalY=0 NormalZ=1 AngleXU=0 Radius=8 StartAngle=4.71239 EndAngle=7.85398
    g57: LineSegment StartX=-36.9468 StartY=8 StartZ=0 EndX=-46.9468 EndY=8 EndZ=0
    g58: LineSegment StartX=-36.9468 StartY=-8 StartZ=0 EndX=-46.9468 EndY=-8 EndZ=0
    g59: ArcOfCircle CenterX=-46.9468 CenterY=-10 CenterZ=0 NormalX=0 NormalY=0 NormalZ=1 AngleXU=0 Radius=2 StartAngle=1.5708 EndAngle=3.35146
    g60: ArcOfCircle CenterX=-46.9468 CenterY=10 CenterZ=0 NormalX=0 NormalY=0 NormalZ=1 AngleXU=0 Radius=2 StartAngle=2.93172 EndAngle=4.71239
    g61: LineSegment [constr] StartX=34 StartY=0 StartZ=0 EndX=46 EndY=0 EndZ=0
  constraints (155):
    c: Coincident(g0,g-3)
    c: Equal(g0,g-3)
    c: Diameter(g3) = 3
    c: Equal(g3,g2)
    c: Equal(g3,g1)
    c: Tangent(g1,g-4)
    c: Coincident(g4,g5)
    c: Coincident(g5,g6)
    c: Coincident(g6,g4)
    c: Equal(g4,g5)
    c: Equal(g4,g6)
    c: PointOnObject(g5,g7)
    c: Coincident(g6,g1)
    c: Coincident(g2,g4)
    c: Coincident(g3,g5)
    c: Coincident(g7,g0)
    c: Tangent(g10,g9) = -1.5708
    c: Tangent(g11,g9) = 1.5708
    c: Diameter(g9) = 4
    c: Diameter(g8) = 12
    c: Tangent(g8,g12) = 1.5708
    c: Tangent(g11,g12) = -1.5708
    c: Tangent(g8,g13) = 1.5708
    c: Tangent(g10,g13) = 1.5708
    c: Radius(g13) = 2
    c: Equal(g13,g12)
    c: Coincident(g14,g15)
    c: Coincident(g15,g16)
    c: Coincident(g16,g17)
    c: Coincident(g17,g14)
    c: Horizontal(g14)
    c: Horizontal(g16)
    c: Vertical(g15)
    c: Vertical(g17)
    c: Coincident(g18,g19)
    c: Coincident(g19,g20)
    c: Coincident(g20,g21)
    c: Coincident(g21,g18)
    c: Horizontal(g18)
    c: Horizontal(g20)
    c: Vertical(g19)
    c: Vertical(g21)
    c: Coincident(g22,g23)
    c: Coincident(g23,g24)
    c: Coincident(g24,g25)
    c: Coincident(g25,g22)
    c: Horizontal(g22)
    c: Horizontal(g24)
    c: Vertical(g23)
    c: Vertical(g25)
    c: Coincident(g26,g27)
    c: Coincident(g27,g28)
    c: Coincident(g28,g29)
    c: Coincident(g29,g26)
    c: Horizontal(g26)
    c: Horizontal(g28)
    c: Vertical(g27)
    c: Vertical(g29)
    c: Coincident(g30,g31)
    c: Coincident(g31,g32)
    c: Coincident(g32,g33)
    c: Coincident(g33,g30)
    c: Horizontal(g30)
    c: Horizontal(g32)
    c: Vertical(g31)
    c: Vertical(g33)
    c: Equal(g16,g15)
    c: Equal(g19,g20)
    c: Equal(g31,g32)
    c: Equal(g24,g23)
    c: Equal(g27,g28)
    c: Equal(g14,g18)
    c: Equal(g18,g30)
    c: Equal(g30,g22)
    c: Equal(g22,g26)
    c: DistanceX(g14,g14) = 10
    c: Vertical(g16,g26)
    c: Vertical(g28,g30)
    c: Horizontal(g26,g18)
    c: Horizontal(g26,g22)
    c: Coincident(g34,g16)
    c: Coincident(g34,g26)
    c: Coincident(g35,g26)
    c: Coincident(g35,g18)
    c: Coincident(g36,g15)
    c: Coincident(g36,g26)
    c: Coincident(g37,g26)
    c: Coincident(g37,g22)
    c: Coincident(g38,g30)
    c: Coincident(g38,g27)
    c: Coincident(g39,g27)
    c: Coincident(g39,g24)
    c: Coincident(g40,g30)
    c: Coincident(g40,g28)
    c: Coincident(g41,g28)
    c: Coincident(g41,g19)
    c: Equal(g34,g40)
    c: Equal(g35,g37)
    c: Equal(g35,g34)
    c: DistanceX(g35,g35) = 4
    c: Tangent(g2,g-4)
    c: Coincident(g42,g43)
    c: Coincident(g43,g44)
    c: Coincident(g44,g45)
    c: Coincident(g45,g42)
    c: Symmetric(g18,g26,g45)
    c: Symmetric(g26,g22,g43)
    c: Symmetric(g15,g26,g42)
    c: Symmetric(g27,g30,g44)
    c: PointOnObject(g46,g44)
    c: Vertical(g46)
    c: PointOnObject(g47,g45)
    c: Horizontal(g47)
    c: Symmetric(g42,g42,g46)
    c: Symmetric(g42,g43,g47)
    c: Coincident(g48,g42)
    c: Coincident(g49,g46)
    c: Coincident(g50,g42)
    c: Coincident(g51,g47)
    c: Coincident(g52,g43)
    c: Coincident(g53,g46)
    c: Coincident(g54,g44)
    c: Coincident(g55,g47)
    c: Equal(g54,g55)
    c: Equal(g55,g48)
    c: Equal(g48,g49)
    c: Equal(g49,g50)
    c: Equal(g50,g52)
    c: Equal(g52,g53)
    c: Equal(g53,g51)
    c: Diameter(g51) = 3
    c: Tangent(g56,g58) = 1.5708
    c: Tangent(g56,g57) = -1.5708
    c: Diameter(g56) = 16
    c: Tangent(g58,g59) = -1.5708
    c: Tangent(g0,g59) = -1.5708
    c: Tangent(g57,g60) = 1.5708
    c: Tangent(g0,g60) = -1.5708
    c: Radius(g60) = 2
    c: Equal(g60,g59)
    c: Tangent(g3,g-4)
    c: Equal(g11,g10)
    c: Parallel(g10,g11)
    c: Horizontal(g8,g9)
    c: Distance(g8,g9) = 12
    c: Coincident(g61,g9)
    c: PointOnObject(g61,g7)
    c: Horizontal(g61)
    c: Distance(g61) = 12
    c: PointOnObject(g9,g-1)
    c: Symmetric(g14,g14,g0)
    c: Parallel(g57,g58)
    c: Symmetric(g56,g56,g-1)
    c: DistanceX(g57,g57) = 10
    c: Horizontal(g9,g2)
FEATURE [PartDesign::Pad] Pad006
  ClaimChildren = false
  Direction = (1,1,1)
  Fit = 0
  FitJoin = 0
  InnerFit = 0
  InnerFitJoin = 0
  InnerTaperAngle = 0
  InnerTaperAngleRev = 0
  Length = 2.9
  Length2 = 100
  NewSolid = false
  Placement = pos=(0,0,-8) rot=(0.707107,0.707107,0;3.14159rad)
  Profile = -> Sketch014
  Suppress = false
  TreeRank = 0
  Type = 0
  _ProfileBasedVersion = 0
  expr: Length = Spreadsheet.acrylic_thickness
FEATURE [Part::FeaturePython] Screw  label="(M3.5)x38-Screw"  # Fasteners workbench fastener (typed FeaturePython)
  Placement = pos=(-39.8372,-23,11.7) rot=(0,0,1;0rad)
  TreeRank = 0
  baseObject = -> Body015 [Edge12]
  diameter = 5
  invert = false
  leftHanded = false
  length = 11
  lengthCustom = 38
  matchOuter = false
  offset = 0
  thread = false
  type = 40
FEATURE [Part::FeaturePython] Screw001  label="(M3.5)x38-Screw309"  # Fasteners workbench fastener (typed FeaturePython)
  Placement = pos=(39.8372,-23,11.7) rot=(0,0,1;0rad)
  TreeRank = 0
  baseObject = -> Body015 [Edge9]
  diameter = 5
  invert = false
  leftHanded = false
  length = 11
  lengthCustom = 38
  matchOuter = false
  offset = 0
  thread = false
  type = 40
FEATURE [Part::FeaturePython] Screw002  label="(M3.5)x38-Screw310"  # Fasteners workbench fastener (typed FeaturePython)
  Placement = pos=(0,46,11.7) rot=(0,0,1;0rad)
  TreeRank = 0
  baseObject = -> Body015 [Edge15]
  diameter = 5
  invert = false
  leftHanded = false
  length = 11
  lengthCustom = 38
  matchOuter = false
  offset = 0
  thread = false
  type = 40
FEATURE [Part::FeaturePython] Nut  label="M3-Nut"  # Fasteners workbench fastener (typed FeaturePython)
  Placement = pos=(-39.8372,-23,-100.9) rot=(-1,0,0;3.14159rad)
  TreeRank = 0
  baseObject = -> Body016 [Edge69]
  diameter = 1
  invert = false
  leftHanded = false
  matchOuter = false
  offset = 0
  thread = false
  type = 9
FEATURE [Part::FeaturePython] Nut001  label="M3-Nut447"  # Fasteners workbench fastener (typed FeaturePython)
  Placement = pos=(39.8372,-23,-100.9) rot=(-1,0,0;3.14159rad)
  TreeRank = 0
  baseObject = -> Body016 [Edge63]
  diameter = 1
  invert = false
  leftHanded = false
  matchOuter = false
  offset = 0
  thread = false
  type = 9
FEATURE [Part::FeaturePython] Nut002  label="M3-Nut448"  # Fasteners workbench fastener (typed FeaturePython)
  Placement = pos=(1e-14,46,-100.9) rot=(-1,0,0;3.14159rad)
  TreeRank = 0
  baseObject = -> Body016 [Edge66]
  diameter = 1
  invert = false
  leftHanded = false
  matchOuter = false
  offset = 0
  thread = false
  type = 9
FEATURE [PartDesign::ShapeBinder] ShapeBinder008
  Placement = pos=(0,0,5) rot=(0,0,1;0rad)
  Support = -> [Body012]
  TraceSupport = false
  TreeRank = 5
FEATURE [PartDesign::Plane] DatumPlane005
  AttachmentSupport = -> [ShapeBinder008]
  Length = 89
  MapMode = 5
  MinimumLength = 10
  MinimumWidth = 10
  Placement = pos=(0,0,-54.1) rot=(0,0,1;0rad)
  ResizeMode = 0
  Support = -> [ShapeBinder008]
  TreeRank = 0
  Width = 89
FEATURE [Sketcher::SketchObject] Sketch011
  ArcFitTolerance = 0
  AttachmentSupport = -> [DatumPlane005]
  ExternalGeometry = -> [ShapeBinder004]
  FullyConstrained = true
  MapMode = 5
  Placement = pos=(0,0,-54.1) rot=(0,0,1;0rad)
  Support = -> [DatumPlane005]
  TreeRank = 0
  sketch-geometry (2):
    g0: Circle CenterX=0 CenterY=0 CenterZ=0 NormalX=0 NormalY=0 NormalZ=1 AngleXU=0 Radius=44.5
    g1: Circle CenterX=0 CenterY=0 CenterZ=0 NormalX=0 NormalY=0 NormalZ=1 AngleXU=0 Radius=38.5
  constraints (4):
    c: Coincident(g0,g-4)
    c: Coincident(g1,g0)
    c: Equal(g1,g-4)
    c: Equal(g-3,g0)
FEATURE [PartDesign::Pad] Pad003
  ClaimChildren = false
  Direction = (1,1,1)
  Fit = 0
  FitJoin = 0
  InnerFit = 0
  InnerFitJoin = 0
  InnerTaperAngle = 0
  InnerTaperAngleRev = 0
  Length = 12.9
  Length2 = 100
  NewSolid = false
  Placement = pos=(0,0,-54.1) rot=(0,0,1;0rad)
  Profile = -> Sketch011
  Suppress = false
  TreeRank = 0
  Type = 0
  _ProfileBasedVersion = 0
  expr: Length = Spreadsheet.led_strip_width + Spreadsheet.acrylic_thickness
FEATURE [PartDesign::Body] Body013  label="Upper_spacer"
  AutoGroupSolids = false
  ClaimAllChildren = false
  ExportMode = 0
  Group = -> [ShapeBinder004,DatumPlane005,Sketch011,Pad003,ShapeBinder008]
  Origin = -> Origin016
  Placement = pos=(0,0,5) rot=(0,0,1;0rad)
  Tip = -> Pad003
  TreeRank = 0
  _ExportChildren = -> [ShapeBinder004,DatumPlane005,Pad003,ShapeBinder008]
  _GroupVersion = 1
FEATURE [PartDesign::ShapeBinder] ShapeBinder009
  Placement = pos=(0,0,5) rot=(0,0,1;0rad)
  Support = -> [Body013]
  TraceSupport = false
  TreeRank = 6
FEATURE [PartDesign::Plane] DatumPlane006
  AttachmentSupport = -> [ShapeBinder009]
  Length = 77.4
  MapMode = 5
  MinimumLength = 10
  MinimumWidth = 10
  Placement = pos=(0,0,-36.2) rot=(0,0,1;0rad)
  ResizeMode = 0
  Support = -> [ShapeBinder009]
  TreeRank = 0
  Width = 77.3484
FEATURE [Sketcher::SketchObject] Sketch012
  ArcFitTolerance = 0
  AttachmentSupport = -> [DatumPlane006]
  ExternalGeometry = -> [ShapeBinder005]
  FullyConstrained = true
  MapMode = 5
  Placement = pos=(0,0,-36.2) rot=(0,0,1;0rad)
  Support = -> [DatumPlane006]
  TreeRank = 0
  sketch-geometry (2):
    g0: Circle CenterX=0 CenterY=0 CenterZ=0 NormalX=0 NormalY=0 NormalZ=1 AngleXU=0 Radius=38.7
    g1: LineSegment [constr] StartX=-38.7 StartY=0 StartZ=0 EndX=-38.5 EndY=0 EndZ=0
  constraints (6):
    c: Coincident(g0,g-3)
    c: PointOnObject(g1,g0)
    c: PointOnObject(g1,g-3)
    c: Horizontal(g1)
    c: PointOnObject(g1,g-1)
    c: DistanceX(g1,g1) = 0.2
FEATURE [PartDesign::Pad] Pad004
  ClaimChildren = false
  Direction = (1,1,1)
  Fit = 0
  FitJoin = 0
  InnerFit = 0
  InnerFitJoin = 0
  InnerTaperAngle = 0
  InnerTaperAngleRev = 0
  Length = 2.9
  Length2 = 100
  NewSolid = false
  Placement = pos=(0,0,-36.2) rot=(0,0,1;0rad)
  Profile = -> Sketch012
  Reversed = true
  Suppress = false
  TreeRank = 0
  Type = 0
  _ProfileBasedVersion = 0
  expr: Length = Spreadsheet.acrylic_thickness
FEATURE [PartDesign::Body] Body014  label="Mirror_one_way"
  AutoGroupSolids = false
  ClaimAllChildren = false
  ExportMode = 0
  Group = -> [ShapeBinder005,DatumPlane006,Sketch012,Pad004,ShapeBinder009]
  Origin = -> Origin017
  Placement = pos=(0,0,5) rot=(0,0,1;0rad)
  Tip = -> Pad004
  TreeRank = 0
  _ExportChildren = -> [ShapeBinder005,DatumPlane006,Pad004,ShapeBinder009]
  _GroupVersion = 1
FEATURE [PartDesign::ShapeBinder] ShapeBinder010
  Placement = pos=(0,0,5) rot=(0,0,1;0rad)
  Support = -> [Body013]
  TraceSupport = false
  TreeRank = 7
FEATURE [PartDesign::Plane] DatumPlane007
  AttachmentSupport = -> [ShapeBinder010]
  Length = 100
  MapMode = 5
  MinimumLength = 10
  MinimumWidth = 10
  Placement = pos=(0,0,-36.2) rot=(0,0,1;0rad)
  ResizeMode = 0
  Support = -> [ShapeBinder010]
  TreeRank = 0
  Width = 99.9333
FEATURE [Sketcher::SketchObject] Sketch013
  ArcFitTolerance = 0
  AttachmentSupport = -> [DatumPlane007]
  ExternalGeometry = -> [ShapeBinder006]
  FullyConstrained = true
  MapMode = 5
  Placement = pos=(0,0,-36.2) rot=(0,0,1;0rad)
  Support = -> [DatumPlane007]
  TreeRank = 0
  expr: Constraints[8] = Spreadsheet.screw_hole_dia
  sketch-geometry (10):
    g0: Circle CenterX=0 CenterY=0 CenterZ=0 NormalX=0 NormalY=0 NormalZ=1 AngleXU=0 Radius=50
    g1: Circle CenterX=0 CenterY=0 CenterZ=0 NormalX=0 NormalY=0 NormalZ=1 AngleXU=0 Radius=37
    g2: LineSegment [constr] StartX=-37 StartY=0 StartZ=0 EndX=-38.5 EndY=0 EndZ=0
    g3: Circle CenterX=0 CenterY=46 CenterZ=0 NormalX=0 NormalY=0 NormalZ=1 AngleXU=0 Radius=1.5
    g4: Circle CenterX=-39.8372 CenterY=-23 CenterZ=0 NormalX=0 NormalY=0 NormalZ=1 AngleXU=0 Radius=1.5
    g5: Circle CenterX=39.8372 CenterY=-23 CenterZ=0 NormalX=0 NormalY=0 NormalZ=1 AngleXU=0 Radius=1.5
    g6: LineSegment [constr] StartX=0 StartY=46 StartZ=0 EndX=-39.8372 EndY=-23 EndZ=0
    g7: LineSegment [constr] StartX=-39.8372 StartY=-23 StartZ=0 EndX=39.8372 EndY=-23 EndZ=0
    g8: LineSegment [constr] StartX=39.8372 StartY=-23 StartZ=0 EndX=0 EndY=46 EndZ=0
    g9: Circle [constr] CenterX=0 CenterY=0 CenterZ=0 NormalX=0 NormalY=0 NormalZ=1 AngleXU=0 Radius=46
  constraints (25):
    c: Coincident(g0,g-4)
    c: Coincident(g1,g0)
    c: Equal(g-3,g0)
    c: PointOnObject(g2,g1)
    c: PointOnObject(g2,g-4)
    c: Horizontal(g2)
    c: PointOnObject(g2,g-1)
    c: DistanceX(g2,g2) = 1.5
    c: Diameter(g4) = 3
    c: Equal(g4,g5)
    c: Equal(g4,g3)
    c: PointOnObject(g3,g-2)
    c: Tangent(g3,g-5)
    c: Coincident(g6,g7)
    c: Coincident(g7,g8)
    c: Coincident(g8,g6)
    c: Equal(g6,g7)
    c: Equal(g6,g8)
    c: PointOnObject(g6,g9)
    c: PointOnObject(g7,g9)
    c: PointOnObject(g8,g9)
    c: Coincident(g9,g0)
    c: Coincident(g8,g3)
    c: Coincident(g4,g6)
    c: Coincident(g5,g7)
FEATURE [PartDesign::Pad] Pad005
  ClaimChildren = false
  Direction = (1,1,1)
  Fit = 0
  FitJoin = 0
  InnerFit = 0
  InnerFitJoin = 0
  InnerTaperAngle = 0
  InnerTaperAngleRev = 0
  Length = 2.9
  Length2 = 100
  NewSolid = false
  Placement = pos=(0,0,-36.2) rot=(0,0,1;0rad)
  Profile = -> Sketch013
  Suppress = false
  TreeRank = 0
  Type = 0
  _ProfileBasedVersion = 0
  expr: Length = Spreadsheet.acrylic_thickness
FEATURE [PartDesign::Body] Body015  label="Front_bezel"
  AutoGroupSolids = false
  ClaimAllChildren = false
  ExportMode = 0
  Group = -> [ShapeBinder006,DatumPlane007,Sketch013,Pad005,ShapeBinder010]
  Origin = -> Origin018
  Placement = pos=(0,0,45) rot=(0,0,1;0rad)
  Tip = -> Pad005
  TreeRank = 0
  _ExportChildren = -> [ShapeBinder006,DatumPlane007,Pad005,ShapeBinder010]
  _GroupVersion = 1
FEATURE [PartDesign::ShapeBinder] ShapeBinder011
  Placement = pos=(0,0,-67) rot=(0,0,1;0rad)
  Support = -> [Body]
  TraceSupport = false
  TreeRank = 8
FEATURE [PartDesign::Body] Body016  label="Back_cover"
  AutoGroupSolids = false
  ClaimAllChildren = false
  ExportMode = 0
  Group = -> [ShapeBinder007,DatumPlane008,Sketch014,Pad006,ShapeBinder011]
  Origin = -> Origin019
  Placement = pos=(0,0,-90) rot=(0,0,1;0rad)
  Tip = -> Pad006
  TreeRank = 0
  _ExportChildren = -> [ShapeBinder007,DatumPlane008,Pad006,ShapeBinder011]
  _GroupVersion = 1
FEATURE [Part::Part2DObjectPython] Shape2DView  label="Back_cover_DXF"  # Draft 2D object (typed FeaturePython)
  Base = -> Body016
  FuseArch = false
  HiddenLines = false
  InPlace = true
  Projection = (0,0,1)
  ProjectionMode = 0
  SegmentLength = 0.05
  Tessellation = false
  TreeRank = 9
  VisibleOnly = false
FEATURE [Part::Part2DObjectPython] Shape2DView001  label="Front_bezel_DXF"  # Draft 2D object (typed FeaturePython)
  Base = -> Body015
  FuseArch = false
  HiddenLines = false
  InPlace = true
  Projection = (0,0,1)
  ProjectionMode = 0
  SegmentLength = 0.05
  Tessellation = false
  TreeRank = 10
  VisibleOnly = false
FEATURE [Part::Part2DObjectPython] Shape2DView002  label="Mirror_one_way_DXF"  # Draft 2D object (typed FeaturePython)
  Base = -> Body014
  FuseArch = false
  HiddenLines = false
  InPlace = true
  Projection = (0,0,1)
  ProjectionMode = 0
  SegmentLength = 0.05
  Tessellation = false
  TreeRank = 11
  VisibleOnly = false
FEATURE [Part::Part2DObjectPython] Shape2DView003  label="Mirror_DXF"  # Draft 2D object (typed FeaturePython)
  Base = -> Body012
  FuseArch = false
  HiddenLines = false
  InPlace = true
  Projection = (0,0,1)
  ProjectionMode = 0
  SegmentLength = 0.05
  Tessellation = false
  TreeRank = 12
  VisibleOnly = false
FEATURE [App::DocumentObjectGroup] Group  label="DXF"
  ClaimAllChildren = true
  ExportMode = 1
  Group = -> [Shape2DView,Shape2DView001,Shape2DView002,Shape2DView003]
  TreeRank = 0
  _GroupVersion = 1
FEATURE [TechDraw::DrawSVGTemplate] Template
  EditableTexts = AUTHOR_NAME=Anool J M,DRAWING_TITLE=Lower Spacer,FC-DATE=02/04/2023,FC-REV=REV A,FC-SC=1:1,FC-SH=1 / 8,FC-SI=A4,FREECAD_DRAWING=77 mm ID, 89 mm OD,+3 more (map truncated)
  Height = 210
  Orientation = 1
  TreeRank = 14
  Width = 297
FEATURE [TechDraw::DrawSVGTemplate] Template001
  EditableTexts = AUTHOR_NAME=Anool J M,DRAWING_TITLE=Upper Spacer,FC-DATE=02/04/2023,FC-REV=REV A,FC-SC=1:1,FC-SH=2 / 8,FC-SI=A4,FREECAD_DRAWING=77 mm ID, 89 mm OD,+3 more (map truncated)
  Height = 210
  Orientation = 1
  TreeRank = 21
  Width = 297
FEATURE [TechDraw::DrawProjGroupItem] ProjItem002  label="Front001"
  CoarseView = false
  Direction = (0,0,1)
  Focus = 100
  HardHidden = true
  IsoCount = 0
  IsoHidden = false
  IsoVisible = false
  LockPosition = true
  Perspective = false
  Rotation = 0
  RotationVector = (1,0,0)
  ScaleType = 2
  SeamHidden = false
  SeamVisible = false
  SmoothHidden = false
  SmoothVisible = true
  Source = -> [Body013]
  TreeRank = 24
  Type = 0
  X = 0
  XDirection = (1,0,0)
  Y = 0
FEATURE [TechDraw::DrawProjGroupItem] ProjItem003  label="Bottom001"
  CoarseView = false
  Direction = (0,-1,0)
  Focus = 100
  HardHidden = true
  IsoCount = 0
  IsoHidden = false
  IsoVisible = false
  LockPosition = false
  Perspective = false
  Rotation = 0
  RotationVector = (1,0,0)
  ScaleType = 2
  SeamHidden = false
  SeamVisible = false
  SmoothHidden = false
  SmoothVisible = true
  Source = -> [Body013]
  TreeRank = 26
  Type = 5
  X = 0
  XDirection = (1,0,0)
  Y = 65.95
FEATURE [TechDraw::DrawProjGroup] ProjGroup001
  Anchor = -> ProjItem002
  AutoDistribute = true
  LockPosition = false
  ProjectionType = 0
  Rotation = 0
  ScaleType = 0
  Source = -> [Body013]
  TreeRank = 25
  Views = -> [ProjItem002,ProjItem003]
  X = 152.158
  Y = 100.518
  spacingX = 15
  spacingY = 15
FEATURE [TechDraw::DrawSVGTemplate] Template002
  EditableTexts = AUTHOR_NAME=Anool J M,DRAWING_TITLE=Mirror, 100%,FC-DATE=02/04/2023,FC-REV=REV A,FC-SC=1:1,FC-SH=3 / 8,FC-SI=A4,FREECAD_DRAWING=100 mm OD,+3 more (map truncated)
  Height = 210
  Orientation = 1
  TreeRank = 28
  Width = 297
FEATURE [TechDraw::DrawProjGroupItem] ProjItem004  label="Front002"
  CoarseView = false
  Direction = (0,0,1)
  Focus = 100
  HardHidden = true
  IsoCount = 0
  IsoHidden = false
  IsoVisible = false
  LockPosition = true
  Perspective = false
  Rotation = 0
  RotationVector = (1,0,0)
  ScaleType = 2
  SeamHidden = false
  SeamVisible = false
  SmoothHidden = false
  SmoothVisible = true
  Source = -> [Body012]
  TreeRank = 31
  Type = 0
  X = 0
  XDirection = (1,0,0)
  Y = 0
FEATURE [TechDraw::DrawProjGroupItem] ProjItem005  label="Right"
  CoarseView = false
  Direction = (1,0,1e-16)
  Focus = 100
  HardHidden = true
  IsoCount = 0
  IsoHidden = false
  IsoVisible = false
  LockPosition = false
  Perspective = false
  Rotation = 0
  RotationVector = (1,0,0)
  ScaleType = 2
  SeamHidden = false
  SeamVisible = false
  SmoothHidden = false
  SmoothVisible = true
  Source = -> [Body012]
  TreeRank = 33
  Type = 2
  X = -66.45
  XDirection = (1e-16,0,-1)
  Y = 0
FEATURE [TechDraw::DrawProjGroup] ProjGroup002
  Anchor = -> ProjItem004
  AutoDistribute = true
  LockPosition = false
  ProjectionType = 0
  Rotation = 0
  ScaleType = 0
  Source = -> [Body012]
  TreeRank = 32
  Views = -> [ProjItem004,ProjItem005]
  X = 103.115
  Y = 122.909
  spacingX = 15
  spacingY = 15
FEATURE [TechDraw::DrawSVGTemplate] Template003
  EditableTexts = AUTHOR_NAME=Anool J M,DRAWING_TITLE=Mirror, one way,FC-DATE=02/04/2023,FC-REV=REV A,FC-SC=1:1,FC-SH=4 / 8,FC-SI=A4,FREECAD_DRAWING=77.4 mm dia,+3 more (map truncated)
  Height = 210
  Orientation = 1
  TreeRank = 35
  Width = 297
FEATURE [TechDraw::DrawProjGroupItem] ProjItem006  label="Front003"
  CoarseView = false
  Direction = (0,0,1)
  Focus = 100
  HardHidden = true
  IsoCount = 0
  IsoHidden = false
  IsoVisible = false
  LockPosition = true
  Perspective = false
  Rotation = 0
  RotationVector = (1,0,0)
  ScaleType = 2
  SeamHidden = false
  SeamVisible = false
  SmoothHidden = false
  SmoothVisible = true
  Source = -> [Body014]
  TreeRank = 38
  Type = 0
  X = 0
  XDirection = (1,0,0)
  Y = 0
FEATURE [TechDraw::DrawProjGroupItem] ProjItem007  label="Right001"
  CoarseView = false
  Direction = (1,0,1e-16)
  Focus = 100
  HardHidden = true
  IsoCount = 0
  IsoHidden = false
  IsoVisible = false
  LockPosition = false
  Perspective = false
  Rotation = 0
  RotationVector = (1,0,0)
  ScaleType = 2
  SeamHidden = false
  SeamVisible = false
  SmoothHidden = false
  SmoothVisible = true
  Source = -> [Body014]
  TreeRank = 40
  Type = 2
  X = -55.15
  XDirection = (1e-16,0,-1)
  Y = 0
FEATURE [TechDraw::DrawProjGroup] ProjGroup003
  Anchor = -> ProjItem006
  AutoDistribute = true
  LockPosition = false
  ProjectionType = 0
  Rotation = 0
  ScaleType = 0
  Source = -> [Body014]
  TreeRank = 39
  Views = -> [ProjItem006,ProjItem007]
  X = 96.828
  Y = 129.074
  spacingX = 15
  spacingY = 15
FEATURE [TechDraw::DrawSVGTemplate] Template004
  EditableTexts = AUTHOR_NAME=Anool J M,DRAWING_TITLE=Front bezel,FC-DATE=02/04/2023,FC-REV=REV A,FC-SC=1:1,FC-SH=5 / 8,FC-SI=A4,FREECAD_DRAWING=100 mm OD, 74 mm ID,+3 more (map truncated)
  Height = 210
  Orientation = 1
  TreeRank = 42
  Width = 297
FEATURE [TechDraw::DrawProjGroupItem] ProjItem008  label="Front004"
  CoarseView = false
  Direction = (0,0,1)
  Focus = 100
  HardHidden = true
  IsoCount = 0
  IsoHidden = false
  IsoVisible = false
  LockPosition = true
  Perspective = false
  Rotation = 0
  RotationVector = (1,0,0)
  ScaleType = 2
  SeamHidden = false
  SeamVisible = false
  SmoothHidden = false
  SmoothVisible = true
  Source = -> [Body015]
  TreeRank = 45
  Type = 0
  X = 0
  XDirection = (1,0,0)
  Y = 0
FEATURE [TechDraw::DrawProjGroupItem] ProjItem009  label="Right002"
  CoarseView = false
  Direction = (1,0,1e-16)
  Focus = 100
  HardHidden = true
  IsoCount = 0
  IsoHidden = false
  IsoVisible = false
  LockPosition = false
  Perspective = false
  Rotation = 0
  RotationVector = (1,0,0)
  ScaleType = 2
  SeamHidden = false
  SeamVisible = false
  SmoothHidden = false
  SmoothVisible = true
  Source = -> [Body015]
  TreeRank = 47
  Type = 2
  X = -66.45
  XDirection = (1e-16,0,-1)
  Y = 0
FEATURE [TechDraw::DrawProjGroup] ProjGroup004
  Anchor = -> ProjItem008
  AutoDistribute = true
  LockPosition = false
  ProjectionType = 0
  Rotation = 0
  ScaleType = 0
  Source = -> [Body015]
  TreeRank = 46
  Views = -> [ProjItem008,ProjItem009]
  X = 107.394
  Y = 122.209
  spacingX = 15
  spacingY = 15
FEATURE [TechDraw::DrawSVGTemplate] Template005
  EditableTexts = AUTHOR_NAME=Anool J M,DRAWING_TITLE=Back cover,FC-DATE=02/04/2023,FC-REV=REV A,FC-SC=1:1,FC-SH=6 / 8,FC-SI=A4,FREECAD_DRAWING=100 mm OD,+3 more (map truncated)
  Height = 210
  Orientation = 1
  TreeRank = 49
  Width = 297
FEATURE [TechDraw::DrawProjGroupItem] ProjItem010  label="Front005"
  CoarseView = false
  Direction = (0,0,1)
  Focus = 100
  HardHidden = true
  IsoCount = 0
  IsoHidden = false
  IsoVisible = false
  LockPosition = true
  Perspective = false
  Rotation = 0
  RotationVector = (1,0,0)
  ScaleType = 2
  SeamHidden = false
  SeamVisible = false
  SmoothHidden = false
  SmoothVisible = true
  Source = -> [Body016]
  TreeRank = 52
  Type = 0
  X = 0
  XDirection = (1,0,0)
  Y = 0
FEATURE [TechDraw::DrawProjGroupItem] ProjItem011  label="Right003"
  CoarseView = false
  Direction = (1,0,1e-16)
  Focus = 100
  HardHidden = true
  IsoCount = 0
  IsoHidden = false
  IsoVisible = false
  LockPosition = false
  Perspective = false
  Rotation = 0
  RotationVector = (1,0,0)
  ScaleType = 2
  SeamHidden = false
  SeamVisible = false
  SmoothHidden = false
  SmoothVisible = true
  Source = -> [Body016]
  TreeRank = 54
  Type = 2
  X = -66.45
  XDirection = (1e-16,0,-1)
  Y = 0
FEATURE [TechDraw::DrawProjGroup] ProjGroup005
  Anchor = -> ProjItem010
  AutoDistribute = true
  LockPosition = false
  ProjectionType = 0
  Rotation = 0
  ScaleType = 0
  Source = -> [Body016]
  TreeRank = 53
  Views = -> [ProjItem010,ProjItem011]
  X = 104.78
  Y = 122.454
  spacingX = 15
  spacingY = 15
FEATURE [TechDraw::DrawViewDimension] Dimension004
  Arbitrary = false
  ArbitraryTolerances = false
  EqualTolerance = true
  FormatSpec = ⌀%.1f
  FormatSpecOverTolerance = %+.1f
  FormatSpecUnderTolerance = %+.1f
  Inverted = false
  LockPosition = false
  MeasureType = 1
  OverTolerance = 0
  References2D = -> [ProjItem002]
  Rotation = 0
  ScaleType = 0
  TheoreticalExact = false
  TreeRank = 59
  Type = 5
  UnderTolerance = 0
  X = 63.4264
  Y = 13.8579
FEATURE [TechDraw::DrawViewDimension] Dimension006
  Arbitrary = false
  ArbitraryTolerances = false
  EqualTolerance = true
  FormatSpec = ⌀%.1f
  FormatSpecOverTolerance = %+.1f
  FormatSpecUnderTolerance = %+.1f
  Inverted = false
  LockPosition = false
  MeasureType = 1
  OverTolerance = 0
  References2D = -> [ProjItem002]
  Rotation = 0
  ScaleType = 0
  TheoreticalExact = false
  TreeRank = 61
  Type = 5
  UnderTolerance = 0
  X = 65.5584
  Y = -11.4594
FEATURE [TechDraw::DrawViewDimension] Dimension007
  Arbitrary = false
  ArbitraryTolerances = false
  EqualTolerance = true
  FormatSpec = %.1f
  FormatSpecOverTolerance = %+.1f
  FormatSpecUnderTolerance = %+.1f
  Inverted = false
  LockPosition = false
  MeasureType = 1
  OverTolerance = 0
  References2D = -> [ProjItem003]
  Rotation = 0
  ScaleType = 0
  TheoreticalExact = false
  TreeRank = 62
  Type = 2
  UnderTolerance = 0
  X = 69.114
  Y = -15.3606
FEATURE [TechDraw::DrawPage] Page001
  KeepUpdated = true
  NextBalloonIndex = 1
  ProjectionType = 0
  Template = -> Template001
  TreeRank = 22
  Views = -> [ProjGroup001,Dimension004,Dimension006,Dimension007]
FEATURE [TechDraw::DrawViewDimension] Dimension008
  Arbitrary = false
  ArbitraryTolerances = false
  EqualTolerance = true
  FormatSpec = ⌀%.1f
  FormatSpecOverTolerance = %+.1f
  FormatSpecUnderTolerance = %+.1f
  Inverted = false
  LockPosition = false
  MeasureType = 1
  OverTolerance = 0
  References2D = -> [ProjItem004]
  Rotation = 0
  ScaleType = 0
  TheoreticalExact = false
  TreeRank = 63
  Type = 5
  UnderTolerance = 0
  X = 71.1548
  Y = 26.1168
FEATURE [TechDraw::DrawViewDimension] Dimension010
  Arbitrary = false
  ArbitraryTolerances = false
  EqualTolerance = true
  FormatSpec = ⌀%.1f
  FormatSpecOverTolerance = %+.1f
  FormatSpecUnderTolerance = %+.1f
  Inverted = false
  LockPosition = false
  MeasureType = 1
  OverTolerance = 0
  References2D = -> [ProjItem004]
  Rotation = 0
  ScaleType = 0
  TheoreticalExact = false
  TreeRank = 65
  Type = 5
  UnderTolerance = 0
  X = 24.5151
  Y = -50.5658
FEATURE [TechDraw::DrawViewDimension] Dimension011
  Arbitrary = false
  ArbitraryTolerances = false
  EqualTolerance = true
  FormatSpec = %.1f
  FormatSpecOverTolerance = %+.1f
  FormatSpecUnderTolerance = %+.1f
  Inverted = false
  LockPosition = false
  MeasureType = 1
  OverTolerance = 0
  References2D = -> [ProjItem004]
  Rotation = 0
  ScaleType = 0
  TheoreticalExact = false
  TreeRank = 66
  Type = 1
  UnderTolerance = 0
  X = -34.341
  Y = -50.7876
FEATURE [TechDraw::DrawViewDimension] Dimension013
  Arbitrary = false
  ArbitraryTolerances = false
  EqualTolerance = true
  FormatSpec = %.1f
  FormatSpecOverTolerance = %+.1f
  FormatSpecUnderTolerance = %+.1f
  Inverted = false
  LockPosition = false
  MeasureType = 1
  OverTolerance = 0
  References2D = -> [ProjItem004]
  Rotation = 0
  ScaleType = 0
  TheoreticalExact = false
  TreeRank = 68
  Type = 0
  UnderTolerance = 0
  X = 12.7683
  Y = -13.6254
FEATURE [TechDraw::DrawViewDimension] Dimension014
  Arbitrary = false
  ArbitraryTolerances = false
  EqualTolerance = true
  FormatSpec = %.1f
  FormatSpecOverTolerance = %+.1f
  FormatSpecUnderTolerance = %+.1f
  Inverted = false
  LockPosition = false
  MeasureType = 1
  OverTolerance = 0
  References2D = -> [ProjItem005]
  Rotation = 0
  ScaleType = 0
  TheoreticalExact = false
  TreeRank = 69
  Type = 1
  UnderTolerance = 0
  X = -19.8097
  Y = -55.1967
FEATURE [TechDraw::DrawViewDimension] Dimension017
  Arbitrary = false
  ArbitraryTolerances = false
  EqualTolerance = true
  FormatSpec = ⌀%.1f
  FormatSpecOverTolerance = %+.1f
  FormatSpecUnderTolerance = %+.1f
  Inverted = false
  LockPosition = false
  MeasureType = 1
  OverTolerance = 0
  References2D = -> [ProjItem006]
  Rotation = 0
  ScaleType = 0
  TheoreticalExact = false
  TreeRank = 72
  Type = 5
  UnderTolerance = 0
  X = 62.6166
  Y = 20.895
FEATURE [TechDraw::DrawViewDimension] Dimension018
  Arbitrary = false
  ArbitraryTolerances = false
  EqualTolerance = true
  FormatSpec = %.1f
  FormatSpecOverTolerance = %+.1f
  FormatSpecUnderTolerance = %+.1f
  Inverted = false
  LockPosition = false
  MeasureType = 1
  OverTolerance = 0
  References2D = -> [ProjItem007]
  Rotation = 0
  ScaleType = 0
  TheoreticalExact = false
  TreeRank = 73
  Type = 1
  UnderTolerance = 0
  X = -26.1168
  Y = -47.7609
FEATURE [TechDraw::DrawPage] Page003
  KeepUpdated = true
  NextBalloonIndex = 1
  ProjectionType = 0
  Template = -> Template003
  TreeRank = 36
  Views = -> [ProjGroup003,Dimension017,Dimension018]
FEATURE [TechDraw::DrawViewDimension] Dimension019
  Arbitrary = false
  ArbitraryTolerances = false
  EqualTolerance = true
  FormatSpec = ⌀%.1f
  FormatSpecOverTolerance = %+.1f
  FormatSpecUnderTolerance = %+.1f
  Inverted = false
  LockPosition = false
  MeasureType = 1
  OverTolerance = 0
  References2D = -> [ProjItem008]
  Rotation = 0
  ScaleType = 0
  TheoreticalExact = false
  TreeRank = 74
  Type = 5
  UnderTolerance = 0
  X = 62.8934
  Y = 18.3883
FEATURE [TechDraw::DrawViewDimension] Dimension020
  Arbitrary = false
  ArbitraryTolerances = false
  EqualTolerance = true
  FormatSpec = ⌀%.1f
  FormatSpecOverTolerance = %+.1f
  FormatSpecUnderTolerance = %+.1f
  Inverted = false
  LockPosition = false
  MeasureType = 1
  OverTolerance = 0
  References2D = -> [ProjItem008]
  Rotation = 0
  ScaleType = 0
  TheoreticalExact = false
  TreeRank = 75
  Type = 5
  UnderTolerance = 0
  X = 64.7589
  Y = -11.7259
FEATURE [TechDraw::DrawViewDimension] Dimension021
  Arbitrary = false
  ArbitraryTolerances = false
  EqualTolerance = true
  FormatSpec = ⌀%.1f
  FormatSpecOverTolerance = %+.1f
  FormatSpecUnderTolerance = %+.1f
  Inverted = false
  LockPosition = false
  MeasureType = 1
  OverTolerance = 0
  References2D = -> [ProjItem008]
  Rotation = 0
  ScaleType = 0
  TheoreticalExact = false
  TreeRank = 76
  Type = 5
  UnderTolerance = 0
  X = 62.8934
  Y = -22.6523
FEATURE [TechDraw::DrawViewDimension] Dimension022
  Arbitrary = false
  ArbitraryTolerances = false
  EqualTolerance = true
  FormatSpec = %.1f
  FormatSpecOverTolerance = %+.1f
  FormatSpecUnderTolerance = %+.1f
  Inverted = false
  LockPosition = false
  MeasureType = 1
  OverTolerance = 0
  References2D = -> [ProjItem008]
  Rotation = 0
  ScaleType = 0
  TheoreticalExact = false
  TreeRank = 77
  Type = 7
  UnderTolerance = 0
  X = -23.8416
  Y = 18.3525
FEATURE [TechDraw::DrawViewDimension] Dimension023
  Arbitrary = false
  ArbitraryTolerances = false
  EqualTolerance = true
  FormatSpec = %.1f
  FormatSpecOverTolerance = %+.1f
  FormatSpecUnderTolerance = %+.1f
  Inverted = false
  LockPosition = false
  MeasureType = 1
  OverTolerance = 0
  References2D = -> [ProjItem009]
  Rotation = 0
  ScaleType = 0
  TheoreticalExact = false
  TreeRank = 78
  Type = 1
  UnderTolerance = 0
  X = -22.0982
  Y = -53.9275
FEATURE [TechDraw::DrawPage] Page004
  KeepUpdated = true
  NextBalloonIndex = 1
  ProjectionType = 0
  Template = -> Template004
  TreeRank = 43
  Views = -> [ProjGroup004,Dimension019,Dimension020,Dimension021,Dimension022,Dimension023]
FEATURE [TechDraw::DrawViewDimension] Dimension024
  Arbitrary = false
  ArbitraryTolerances = false
  EqualTolerance = true
  FormatSpec = ⌀%.1f
  FormatSpecOverTolerance = %+.1f
  FormatSpecUnderTolerance = %+.1f
  Inverted = false
  LockPosition = false
  MeasureType = 1
  OverTolerance = 0
  References2D = -> [ProjItem004]
  Rotation = 0
  ScaleType = 0
  TheoreticalExact = false
  TreeRank = 84
  Type = 5
  UnderTolerance = 0
  X = 56.3758
  Y = -25.651
FEATURE [TechDraw::DrawViewDimension] Dimension025
  Arbitrary = false
  ArbitraryTolerances = false
  EqualTolerance = true
  FormatSpec = %.1f
  FormatSpecOverTolerance = %+.1f
  FormatSpecUnderTolerance = %+.1f
  Inverted = false
  LockPosition = false
  MeasureType = 1
  OverTolerance = 0
  References2D = -> [ProjItem004]
  Rotation = 0
  ScaleType = 0
  TheoreticalExact = false
  TreeRank = 85
  Type = 7
  UnderTolerance = 0
  X = -24.9423
  Y = 23.4151
FEATURE [TechDraw::DrawViewDimension] Dimension026
  Arbitrary = false
  ArbitraryTolerances = false
  EqualTolerance = true
  FormatSpec = %.1f
  FormatSpecOverTolerance = %+.1f
  FormatSpecUnderTolerance = %+.1f
  Inverted = false
  LockPosition = false
  MeasureType = 1
  OverTolerance = 0
  References2D = -> [ProjItem004]
  Rotation = 0
  ScaleType = 0
  TheoreticalExact = false
  TreeRank = 86
  Type = 2
  UnderTolerance = 0
  X = 12.866
  Y = 24.4265
FEATURE [TechDraw::DrawHatch] Hatch004  label="Hatch004F0"
  HatchPattern = <path>
  Source = -> ProjItem002 [Face0]
  TreeRank = 90
FEATURE [TechDraw::DrawProjGroupItem] ProjItem012  label="Front006"
  CoarseView = false
  Direction = (0,0,-1)
  Focus = 100
  HardHidden = true
  IsoCount = 0
  IsoHidden = false
  IsoVisible = false
  LockPosition = true
  Perspective = false
  Rotation = 0
  RotationVector = (-1,0,0)
  ScaleType = 2
  SeamHidden = false
  SeamVisible = false
  SmoothHidden = false
  SmoothVisible = true
  Source = -> [Body]
  TreeRank = 92
  Type = 0
  X = 0
  XDirection = (-1,0,0)
  Y = 0
FEATURE [TechDraw::DrawProjGroupItem] ProjItem013  label="Bottom002"
  CoarseView = false
  Direction = (0,-1,0)
  Focus = 100
  HardHidden = true
  IsoCount = 0
  IsoHidden = false
  IsoVisible = false
  LockPosition = false
  Perspective = false
  Rotation = 0
  RotationVector = (1,0,0)
  ScaleType = 2
  SeamHidden = false
  SeamVisible = false
  SmoothHidden = false
  SmoothVisible = true
  Source = -> [Body]
  TreeRank = 94
  Type = 5
  X = 0
  XDirection = (-1,0,0)
  Y = 66
FEATURE [TechDraw::DrawProjGroup] ProjGroup006
  Anchor = -> ProjItem012
  AutoDistribute = true
  LockPosition = false
  ProjectionType = 0
  Rotation = 0
  ScaleType = 0
  Source = -> [Body]
  TreeRank = 93
  Views = -> [ProjItem012,ProjItem013]
  X = 153.555
  Y = 100.537
  spacingX = 15
  spacingY = 15
FEATURE [TechDraw::DrawViewDimension] Dimension028
  Arbitrary = false
  ArbitraryTolerances = false
  EqualTolerance = true
  FormatSpec = ⌀%.1f
  FormatSpecOverTolerance = %+.1f
  FormatSpecUnderTolerance = %+.1f
  Inverted = false
  LockPosition = false
  MeasureType = 1
  OverTolerance = 0
  References2D = -> [ProjItem012]
  Rotation = 0
  ScaleType = 0
  TheoreticalExact = false
  TreeRank = 95
  Type = 5
  UnderTolerance = 0
  X = 62.8934
  Y = 16.7893
FEATURE [TechDraw::DrawViewDimension] Dimension029
  Arbitrary = false
  ArbitraryTolerances = false
  EqualTolerance = true
  FormatSpec = ⌀%.1f
  FormatSpecOverTolerance = %+.1f
  FormatSpecUnderTolerance = %+.1f
  Inverted = false
  LockPosition = false
  MeasureType = 1
  OverTolerance = 0
  References2D = -> [ProjItem012]
  Rotation = 0
  ScaleType = 0
  TheoreticalExact = false
  TreeRank = 96
  Type = 5
  UnderTolerance = 0
  X = 61.8274
  Y = -14.9239
FEATURE [TechDraw::DrawViewDimension] Dimension030
  Arbitrary = false
  ArbitraryTolerances = false
  EqualTolerance = true
  FormatSpec = %.1f
  FormatSpecOverTolerance = %+.1f
  FormatSpecUnderTolerance = %+.1f
  Inverted = false
  LockPosition = false
  MeasureType = 1
  OverTolerance = 0
  References2D = -> [ProjItem013]
  Rotation = 0
  ScaleType = 0
  TheoreticalExact = false
  TreeRank = 97
  Type = 2
  UnderTolerance = 0
  X = 61.9074
  Y = -13.9278
FEATURE [TechDraw::DrawViewDimension] Dimension031
  Arbitrary = false
  ArbitraryTolerances = false
  EqualTolerance = true
  FormatSpec = %.1f
  FormatSpecOverTolerance = %+.1f
  FormatSpecUnderTolerance = %+.1f
  Inverted = false
  LockPosition = false
  MeasureType = 1
  OverTolerance = 0
  References2D = -> [ProjItem013]
  Rotation = 0
  ScaleType = 0
  TheoreticalExact = false
  TreeRank = 98
  Type = 1
  UnderTolerance = 0
  X = -32.9868
  Y = 21.5501
FEATURE [TechDraw::DrawViewDimension] Dimension032
  Arbitrary = false
  ArbitraryTolerances = false
  EqualTolerance = true
  FormatSpec = R%.1f
  FormatSpecOverTolerance = %+.1f
  FormatSpecUnderTolerance = %+.1f
  Inverted = false
  LockPosition = false
  MeasureType = 1
  OverTolerance = 0
  References2D = -> [ProjItem013]
  Rotation = 0
  ScaleType = 0
  TheoreticalExact = false
  TreeRank = 99
  Type = 4
  UnderTolerance = 0
  X = 24.0325
  Y = 21.459
FEATURE [TechDraw::DrawHatch] Hatch005  label="Hatch005F2"
  HatchPattern = <path>
  Source = -> ProjItem012 [Face2]
  TreeRank = 100
FEATURE [TechDraw::DrawHatch] Hatch  label="HatchF0"
  HatchPattern = <path>
  Source = -> ProjItem004 [Face0]
  TreeRank = 101
FEATURE [TechDraw::DrawHatch] Hatch006  label="Hatch006F0"
  HatchPattern = <path>
  Source = -> ProjItem006 [Face0]
  TreeRank = 102
FEATURE [TechDraw::DrawHatch] Hatch007  label="Hatch007F0"
  HatchPattern = <path>
  Source = -> ProjItem008 [Face0]
  TreeRank = 103
FEATURE [TechDraw::DrawHatch] Hatch008  label="Hatch008F0"
  HatchPattern = <path>
  Source = -> ProjItem010 [Face0]
  TreeRank = 104
FEATURE [TechDraw::DrawViewDimension] Dimension
  Arbitrary = false
  ArbitraryTolerances = false
  EqualTolerance = true
  FormatSpec = ⌀%.1f
  FormatSpecOverTolerance = %+.1f
  FormatSpecUnderTolerance = %+.1f
  Inverted = false
  LockPosition = false
  MeasureType = 1
  OverTolerance = 0
  References2D = -> [ProjItem010]
  Rotation = 0
  ScaleType = 0
  TheoreticalExact = false
  TreeRank = 105
  Type = 5
  UnderTolerance = 0
  X = 66.6162
  Y = -19.8953
FEATURE [TechDraw::DrawViewDimension] Dimension033
  Arbitrary = false
  ArbitraryTolerances = false
  EqualTolerance = true
  FormatSpec = ⌀%.1f
  FormatSpecOverTolerance = %+.1f
  FormatSpecUnderTolerance = %+.1f
  Inverted = false
  LockPosition = false
  MeasureType = 1
  OverTolerance = 0
  References2D = -> [ProjItem010]
  Rotation = 0
  ScaleType = 0
  TheoreticalExact = false
  TreeRank = 106
  Type = 5
  UnderTolerance = 0
  X = 64.6654
  Y = -29.0982
FEATURE [TechDraw::DrawViewDimension] Dimension034
  Arbitrary = false
  ArbitraryTolerances = false
  EqualTolerance = true
  FormatSpec = %.1f
  FormatSpecOverTolerance = %+.1f
  FormatSpecUnderTolerance = %+.1f
  Inverted = false
  LockPosition = false
  MeasureType = 1
  OverTolerance = 0
  References2D = -> [ProjItem010]
  Rotation = 0
  ScaleType = 0
  TheoreticalExact = false
  TreeRank = 107
  Type = 7
  UnderTolerance = 0
  X = -28.0652
  Y = 21.8844
FEATURE [TechDraw::DrawViewDimension] Dimension035
  Arbitrary = false
  ArbitraryTolerances = false
  EqualTolerance = true
  FormatSpec = ⌀%.1f
  FormatSpecOverTolerance = %+.1f
  FormatSpecUnderTolerance = %+.1f
  Inverted = false
  LockPosition = false
  MeasureType = 1
  OverTolerance = 0
  References2D = -> [ProjItem010]
  Rotation = 0
  ScaleType = 0
  TheoreticalExact = false
  TreeRank = 108
  Type = 5
  UnderTolerance = 0
  X = 65.5907
  Y = -39.2231
FEATURE [TechDraw::DrawViewDimension] Dimension036
  Arbitrary = false
  ArbitraryTolerances = false
  EqualTolerance = true
  FormatSpec = ⌀%.1f
  FormatSpecOverTolerance = %+.1f
  FormatSpecUnderTolerance = %+.1f
  Inverted = false
  LockPosition = false
  MeasureType = 1
  OverTolerance = 0
  References2D = -> [ProjItem010]
  Rotation = 0
  ScaleType = 0
  TheoreticalExact = false
  TreeRank = 109
  Type = 5
  UnderTolerance = 0
  X = 64.0195
  Y = 14.4713
FEATURE [TechDraw::DrawViewDimension] Dimension037
  Arbitrary = false
  ArbitraryTolerances = false
  EqualTolerance = true
  FormatSpec = ⌀%.1f
  FormatSpecOverTolerance = %+.1f
  FormatSpecUnderTolerance = %+.1f
  Inverted = false
  LockPosition = false
  MeasureType = 1
  OverTolerance = 0
  References2D = -> [ProjItem010]
  Rotation = 0
  ScaleType = 0
  TheoreticalExact = false
  TreeRank = 110
  Type = 5
  UnderTolerance = 0
  X = 35.7697
  Y = 55.2393
FEATURE [TechDraw::DrawViewDimension] Dimension038
  Arbitrary = false
  ArbitraryTolerances = false
  EqualTolerance = true
  FormatSpec = %.1f
  FormatSpecOverTolerance = %+.1f
  FormatSpecUnderTolerance = %+.1f
  Inverted = false
  LockPosition = false
  MeasureType = 1
  OverTolerance = 0
  References2D = -> [ProjItem010]
  Rotation = 0
  ScaleType = 0
  TheoreticalExact = false
  TreeRank = 111
  Type = 2
  UnderTolerance = 0
  X = 61.4452
  Y = 29.5696
FEATURE [TechDraw::DrawViewDimension] Dimension039
  Arbitrary = false
  ArbitraryTolerances = false
  EqualTolerance = true
  FormatSpec = %.1f
  FormatSpecOverTolerance = %+.1f
  FormatSpecUnderTolerance = %+.1f
  Inverted = false
  LockPosition = false
  MeasureType = 1
  OverTolerance = 0
  References2D = -> [ProjItem010]
  Rotation = 0
  ScaleType = 0
  TheoreticalExact = false
  TreeRank = 112
  Type = 2
  UnderTolerance = 0
  X = 64.9829
  Y = 5.38449
FEATURE [TechDraw::DrawViewDimension] Dimension040
  Arbitrary = false
  ArbitraryTolerances = false
  EqualTolerance = true
  FormatSpec = R%.1f
  FormatSpecOverTolerance = %+.1f
  FormatSpecUnderTolerance = %+.1f
  Inverted = false
  LockPosition = false
  MeasureType = 1
  OverTolerance = 0
  References2D = -> [ProjItem010]
  Rotation = 0
  ScaleType = 0
  TheoreticalExact = false
  TreeRank = 113
  Type = 4
  UnderTolerance = 0
  X = 15.7494
  Y = -52.0879
FEATURE [TechDraw::DrawViewDimension] Dimension041
  Arbitrary = false
  ArbitraryTolerances = false
  EqualTolerance = true
  FormatSpec = %.1f
  FormatSpecOverTolerance = %+.1f
  FormatSpecUnderTolerance = %+.1f
  Inverted = false
  LockPosition = false
  MeasureType = 1
  OverTolerance = 0
  References2D = -> [ProjItem010]
  Rotation = 0
  ScaleType = 0
  TheoreticalExact = false
  TreeRank = 114
  Type = 2
  UnderTolerance = 0
  X = 23.4221
  Y = -14.6945
FEATURE [TechDraw::DrawViewDimension] Dimension042
  Arbitrary = false
  ArbitraryTolerances = false
  EqualTolerance = true
  FormatSpec = %.1f
  FormatSpecOverTolerance = %+.1f
  FormatSpecUnderTolerance = %+.1f
  Inverted = false
  LockPosition = false
  MeasureType = 1
  OverTolerance = 0
  References2D = -> [ProjItem011]
  Rotation = 0
  ScaleType = 0
  TheoreticalExact = false
  TreeRank = 115
  Type = 1
  UnderTolerance = 0
  X = -22.2768
  Y = -58.3946
FEATURE [PartDesign::ShapeBinder] ShapeBinder012
  Placement = pos=(4e-16,-4e-16,-2.9) rot=(0,0,1;0rad)
  Support = -> [Pad006]
  TraceSupport = false
  TreeRank = 190
FEATURE [Sketcher::SketchObject] Sketch015
  ArcFitTolerance = 1e-06
  AttachmentSupport = -> [ShapeBinder012]
  ExternalGeometry = -> [ShapeBinder012]
  FullyConstrained = true
  MapMode = 5
  Placement = pos=(-3e-16,3e-16,-10.9) rot=(1,0,0;3.14159rad)
  Support = -> [ShapeBinder012]
  TreeRank = 191
  sketch-geometry (28):
    g0: LineSegment StartX=-24 StartY=5 StartZ=0 EndX=-14 EndY=5 EndZ=0
    g1: LineSegment StartX=-14 StartY=5 StartZ=0 EndX=-14 EndY=-5 EndZ=0
    g2: LineSegment StartX=-14 StartY=-5 StartZ=0 EndX=-24 EndY=-5 EndZ=0
    g3: LineSegment StartX=-24 StartY=-5 StartZ=0 EndX=-24 EndY=5 EndZ=0
    g4: LineSegment StartX=-24 StartY=19 StartZ=0 EndX=-14 EndY=19 EndZ=0
    g5: LineSegment StartX=-14 StartY=19 StartZ=0 EndX=-14 EndY=9 EndZ=0
    g6: LineSegment StartX=-14 StartY=9 StartZ=0 EndX=-24 EndY=9 EndZ=0
    g7: LineSegment StartX=-24 StartY=9 StartZ=0 EndX=-24 EndY=19 EndZ=0
    g8: LineSegment StartX=-38 StartY=5 StartZ=0 EndX=-28 EndY=5 EndZ=0
    g9: LineSegment StartX=-28 StartY=5 StartZ=0 EndX=-28 EndY=-5 EndZ=0
    g10: LineSegment StartX=-28 StartY=-5 StartZ=0 EndX=-38 EndY=-5 EndZ=0
    g11: LineSegment StartX=-38 StartY=-5 StartZ=0 EndX=-38 EndY=5 EndZ=0
    g12: LineSegment StartX=-24 StartY=-9 StartZ=0 EndX=-14 EndY=-9 EndZ=0
    g13: LineSegment StartX=-14 StartY=-9 StartZ=0 EndX=-14 EndY=-19 EndZ=0
    g14: LineSegment StartX=-14 StartY=-19 StartZ=0 EndX=-24 EndY=-19 EndZ=0
    g15: LineSegment StartX=-24 StartY=-19 StartZ=0 EndX=-24 EndY=-9 EndZ=0
    g16: LineSegment StartX=-10 StartY=5 StartZ=0 EndX=-2.13e-14 EndY=5 EndZ=0
    g17: LineSegment StartX=-2.16e-14 StartY=5 StartZ=0 EndX=-2.16e-14 EndY=-5 EndZ=0
    g18: LineSegment StartX=-2.16e-14 StartY=-5 StartZ=0 EndX=-10 EndY=-5 EndZ=0
    g19: LineSegment StartX=-10 StartY=-5 StartZ=0 EndX=-10 EndY=5 EndZ=0
    g20: LineSegment [constr] StartX=-28 StartY=5 StartZ=0 EndX=-24 EndY=5 EndZ=0
    g21: LineSegment [constr] StartX=-14 StartY=5 StartZ=0 EndX=-10 EndY=5 EndZ=0
    g22: LineSegment [constr] StartX=-24 StartY=9 StartZ=0 EndX=-24 EndY=5 EndZ=0
    g23: LineSegment [constr] StartX=-24 StartY=-5 StartZ=0 EndX=-24 EndY=-9 EndZ=0
    g24: LineSegment [constr] StartX=-19 StartY=7 StartZ=0 EndX=-19 EndY=9 EndZ=0
    g25: LineSegment [constr] StartX=-19 StartY=7 StartZ=0 EndX=-19 EndY=5 EndZ=0
    g26: LineSegment [constr] StartX=-24 StartY=-4.5e-15 StartZ=0 EndX=-26 EndY=-4.5e-15 EndZ=0
    g27: LineSegment [constr] StartX=-26 StartY=-4.5e-15 StartZ=0 EndX=-28 EndY=-4.5e-15 EndZ=0
  constraints (79):
    c: Coincident(g0,g1)
    c: Coincident(g1,g2)
    c: Coincident(g2,g3)
    c: Coincident(g3,g0)
    c: Horizontal(g0)
    c: Horizontal(g2)
    c: Vertical(g1)
    c: Coincident(g4,g5)
    c: Coincident(g5,g6)
    c: Coincident(g6,g7)
    c: Coincident(g7,g4)
    c: Horizontal(g4)
    c: Horizontal(g6)
    c: Vertical(g5)
    c: Vertical(g7)
    c: Coincident(g8,g9)
    c: Coincident(g9,g10)
    c: Coincident(g10,g11)
    c: Coincident(g11,g8)
    c: Horizontal(g8)
    c: Horizontal(g10)
    c: Vertical(g9)
    c: Vertical(g11)
    c: Coincident(g12,g13)
    c: Coincident(g13,g14)
    c: Coincident(g14,g15)
    c: Coincident(g15,g12)
    c: Horizontal(g12)
    c: Horizontal(g14)
    c: Vertical(g13)
    c: Vertical(g15)
    c: Coincident(g16,g17)
    c: Coincident(g17,g18)
    c: Coincident(g18,g19)
    c: Coincident(g19,g16)
    c: Horizontal(g16)
    c: Horizontal(g18)
    c: Vertical(g17)
    c: Vertical(g19)
    c: Equal(g13,g12)
    c: Equal(g12,g1)
    c: Equal(g1,g0)
    c: Equal(g0,g5)
    c: Equal(g5,g4)
    c: Equal(g4,g17)
    c: Equal(g17,g16)
    c: Equal(g16,g9)
    c: Equal(g9,g8)
    c: Horizontal(g8,g0)
    c: Horizontal(g0,g16)
    c: Vertical(g5,g0)
    c: Vertical(g1,g12)
    c: Coincident(g20,g8)
    c: Coincident(g20,g0)
    c: Coincident(g21,g0)
    c: Coincident(g21,g16)
    c: Coincident(g22,g6)
    c: Coincident(g22,g0)
    c: Coincident(g23,g2)
    c: Coincident(g23,g12)
    c: Equal(g23,g22)
    c: Equal(g22,g20)
    c: Equal(g20,g21)
    c: Symmetric(g0,g2,g-1)
    c: Coincident(g24,g-4)
    c: PointOnObject(g24,g6)
    c: Vertical(g24)
    c: Coincident(g25,g-4)
    c: PointOnObject(g25,g0)
    c: Vertical(g25)
    c: Equal(g25,g24)
    c: Coincident(g26,g-6)
    c: Horizontal(g26)
    c: Coincident(g27,g-6)
    c: Horizontal(g27)
    c: Equal(g27,g26)
    c: PointOnObject(g26,g3)
    c: PointOnObject(g27,g9)
    c: DistanceX(g8,g8) = 10
FEATURE [PartDesign::Pad] Pad007
  ClaimChildren = false
  Direction = (1,1,1)
  Fit = 0
  FitJoin = 0
  InnerFit = 0
  InnerFitJoin = 0
  InnerTaperAngle = 0
  InnerTaperAngleRev = 0
  Length = 0.2
  Length2 = 100
  Linearize = true
  NewSolid = false
  Placement = pos=(4e-16,-4e-16,-2.9) rot=(0,0,1;0rad)
  Profile = -> Sketch015
  Suppress = false
  TreeRank = 192
  Type = 0
  _ProfileBasedVersion = 1
FEATURE [PartDesign::Body] Body017  label="Copper_pads"
  AutoGroupSolids = false
  ClaimAllChildren = false
  ExportMode = 0
  Group = -> [ShapeBinder012,Sketch015,Pad007]
  Origin = -> Origin020
  Placement = pos=(-7.1e-15,0,-95) rot=(0,0,1;0rad)
  Tip = -> Pad007
  TreeRank = 189
  _ExportChildren = -> [ShapeBinder012,Pad007]
  _GroupVersion = 1
FEATURE [Part::Feature] trajectory_line
  TreeRank = 203
  shape: bbox 79.67 x 69 x 85 mm, 0 faces, 0 solids (baked)
FEATURE [App::DocumentObjectGroupPython] BoltGroup  # scripted group (container) (typed FeaturePython)
  AnimationStepTime = 0
  AnimationSteps = 85
  ClaimAllChildren = true
  Distance = 85
  ExportMode = 0
  Group = -> [trajectory_line]
  Revolutions = 0
  TreeRank = 223
  _GroupVersion = 1
FEATURE [Part::Feature] trajectory_line001
  TreeRank = 204
  shape: bbox 2e-07 x 2e-07 x 42 mm, 0 faces, 0 solids (baked)
FEATURE [App::DocumentObjectGroupPython] SimpleGroup  # scripted group (container) (typed FeaturePython)
  AnimationStepTime = 0
  AnimationSteps = 42
  ClaimAllChildren = true
  Distance = 42
  ExportMode = 0
  Group = -> [trajectory_line001]
  Revolutions = 0
  TreeRank = 224
  _GroupVersion = 1
FEATURE [Part::Feature] trajectory_line002
  TreeRank = 205
  shape: bbox 2e-07 x 2e-07 x 75 mm, 0 faces, 0 solids (baked)
FEATURE [App::DocumentObjectGroupPython] SimpleGroup001  # scripted group (container) (typed FeaturePython)
  AnimationStepTime = 0
  AnimationSteps = 75
  ClaimAllChildren = true
  Distance = 75
  ExportMode = 0
  Group = -> [trajectory_line002]
  Revolutions = 0
  TreeRank = 226
  _GroupVersion = 1
FEATURE [Part::Feature] trajectory_line003
  TreeRank = 206
  shape: bbox 2e-07 x 2e-07 x 35 mm, 0 faces, 0 solids (baked)
FEATURE [App::DocumentObjectGroupPython] SimpleGroup002  # scripted group (container) (typed FeaturePython)
  AnimationStepTime = 0
  AnimationSteps = 35
  ClaimAllChildren = true
  Distance = 35
  ExportMode = 0
  Group = -> [trajectory_line003]
  Revolutions = 0
  TreeRank = 227
  _GroupVersion = 1
FEATURE [Part::Feature] trajectory_line004
  TreeRank = 207
  shape: bbox 2e-07 x 2e-07 x 30 mm, 0 faces, 0 solids (baked)
FEATURE [App::DocumentObjectGroupPython] SimpleGroup003  # scripted group (container) (typed FeaturePython)
  AnimationStepTime = 0
  AnimationSteps = 30
  ClaimAllChildren = true
  Distance = 30
  ExportMode = 0
  Group = -> [trajectory_line004]
  Revolutions = 0
  TreeRank = 228
  _GroupVersion = 1
FEATURE [Part::Feature] trajectory_line005
  TreeRank = 208
  shape: bbox 2e-07 x 2e-07 x 25 mm, 0 faces, 0 solids (baked)
FEATURE [App::DocumentObjectGroupPython] SimpleGroup004  # scripted group (container) (typed FeaturePython)
  AnimationStepTime = 0
  AnimationSteps = 25
  ClaimAllChildren = true
  Distance = 25
  ExportMode = 0
  Group = -> [trajectory_line005]
  Revolutions = 0
  TreeRank = 229
  _GroupVersion = 1
FEATURE [Part::Feature] trajectory_line006
  TreeRank = 209
  shape: bbox 2e-07 x 2e-07 x 20 mm, 0 faces, 0 solids (baked)
FEATURE [App::DocumentObjectGroupPython] SimpleGroup005  # scripted group (container) (typed FeaturePython)
  AnimationStepTime = 0
  AnimationSteps = 20
  ClaimAllChildren = true
  Distance = 20
  ExportMode = 0
  Group = -> [trajectory_line006]
  Revolutions = 0
  TreeRank = 230
  _GroupVersion = 1
FEATURE [Part::Feature] trajectory_line007
  TreeRank = 201
  shape: bbox 2e-07 x 2e-07 x 20 mm, 0 faces, 0 solids (baked)
FEATURE [App::DocumentObjectGroupPython] SimpleGroup006  # scripted group (container) (typed FeaturePython)
  AnimationStepTime = 0
  AnimationSteps = 20
  ClaimAllChildren = true
  Distance = 44
  ExportMode = 0
  Group = -> [trajectory_line007]
  Revolutions = 0
  TreeRank = 225
  _GroupVersion = 0
FEATURE [App::DocumentObjectGroupPython] ExplodedAssembly  # scripted group (container) (typed FeaturePython)
  AnimationStep = 0
  ClaimAllChildren = true
  CurrentTrajectory = 0
  ExportMode = 0
  Group = -> [BoltGroup,SimpleGroup006,SimpleGroup,SimpleGroup001,SimpleGroup002,SimpleGroup003,SimpleGroup004,SimpleGroup005]
  InAnimation = false
  RemoveAllTrajectories = false
  ResetAnimation = false
  TreeRank = 231
  _GroupVersion = 0
FEATURE [TechDraw::DrawViewBalloon] Balloon
  BubbleShape = 3
  EndType = 0
  EndTypeScale = 1
  KinkLength = 5
  LockPosition = false
  OriginX = -0.585442
  OriginY = 2.42218
  Rotation = 0
  ScaleType = 0
  ShapeScale = 1
  SourceView = -> ProjItem013
  Text = Slot to allow entry for micro USB connector
  TextWrapLen = 50
  TreeRank = 232
  X = -87.7174
  Y = -30.6108
FEATURE [TechDraw::DrawPage] Page
  KeepUpdated = true
  NextBalloonIndex = 2
  ProjectionType = 0
  Template = -> Template
  TreeRank = 15
  Views = -> [ProjGroup006,Dimension028,Dimension029,Dimension030,Dimension031,Dimension032,Balloon]
FEATURE [TechDraw::DrawViewBalloon] Balloon001
  BubbleShape = 3
  EndType = 0
  EndTypeScale = 1
  KinkLength = 5
  LockPosition = false
  OriginX = -1.04631
  OriginY = -34.9651
  Rotation = 0
  ScaleType = 0
  ShapeScale = 1
  SourceView = -> ProjItem004
  Text = Slot to pass through wiring between ESP32 and LED strip
  TextWrapLen = 60
  TreeRank = 233
  X = 110.31
  Y = -44.5826
FEATURE [TechDraw::DrawPage] Page002
  KeepUpdated = true
  NextBalloonIndex = 2
  ProjectionType = 0
  Template = -> Template002
  TreeRank = 29
  Views = -> [ProjGroup002,Dimension008,Dimension010,Dimension011,Dimension013,Dimension014,Dimension024,Dimension025,Dimension026,Balloon001]
FEATURE [TechDraw::DrawViewBalloon] Balloon002
  BubbleShape = 3
  EndType = 0
  EndTypeScale = 1
  KinkLength = 5
  LockPosition = false
  OriginX = -1.11252
  OriginY = 26.2516
  Rotation = 0
  ScaleType = 0
  ShapeScale = 1
  SourceView = -> ProjItem010
  Text = Keyhole slot for wall hanging
  TextWrapLen = 60
  TreeRank = 234
  X = 93.9065
  Y = 50.3823
FEATURE [TechDraw::DrawViewBalloon] Balloon003
  BubbleShape = 3
  EndType = 0
  EndTypeScale = 1
  KinkLength = 5
  LockPosition = false
  OriginX = -0.391116
  OriginY = -34.1772
  Rotation = 0
  ScaleType = 0
  ShapeScale = 1
  SourceView = -> ProjItem010
  Text = Slot to allow micro USB connector
  TextWrapLen = 60
  TreeRank = 235
  X = 94.8944
  Y = -56.5947
FEATURE [TechDraw::DrawViewBalloon] Balloon004
  BubbleShape = 3
  EndType = 0
  EndTypeScale = 1
  KinkLength = 5
  LockPosition = false
  OriginX = -20.1563
  OriginY = -1.75334
  Rotation = 0
  ScaleType = 0
  ShapeScale = 1
  SourceView = -> ProjItem010
  Text = Holes for wire connections between ESP32 and copper touch pads on back cover
  TextWrapLen = 100
  TreeRank = 236
  X = 118.879
  Y = -9.95765
FEATURE [TechDraw::DrawPage] Page005
  KeepUpdated = true
  NextBalloonIndex = 5
  ProjectionType = 0
  Template = -> Template005
  TreeRank = 50
  Views = -> [ProjGroup005,Dimension,Dimension033,Dimension034,Dimension035,Dimension036,Dimension037,Dimension038,Dimension039,Dimension040,Dimension041,Dimension042,Balloon002,Balloon003,Balloon004]
FEATURE [App::DocumentObjectGroup] Group002  label="Fasteners"
  ClaimAllChildren = true
  ExportMode = 1
  Group = -> [Screw,Screw001,Screw002,Nut,Nut001,Nut002]
  TreeRank = 238
  _GroupVersion = 1
FEATURE [TechDraw::DrawSVGTemplate] Template006
  EditableTexts = AUTHOR_NAME=Anool J M,DRAWING_TITLE=Touch Pads,FC-DATE=02/04/2023,FC-REV=REV A,FC-SC=1:1,FC-SH=7 / 8,FC-SI=A4,FREECAD_DRAWING=Line2,Line1=Line1,+2 more (map truncated)
  Height = 210
  Orientation = 1
  TreeRank = 240
  Width = 297
FEATURE [TechDraw::DrawViewPart] View
  CoarseView = false
  Direction = (0,0,-1)
  Focus = 100
  HardHidden = true
  IsoCount = 0
  IsoHidden = false
  IsoVisible = false
  LockPosition = false
  Perspective = false
  Rotation = 0
  ScaleType = 0
  SeamHidden = false
  SeamVisible = false
  SmoothHidden = false
  SmoothVisible = true
  Source = -> [ShapeBinder012,Pad007]
  TreeRank = 248
  X = 78.9749
  XDirection = (-1,0,0)
  Y = 124.672
FEATURE [TechDraw::DrawHatch] Hatch009  label="Hatch009F5"
  HatchPattern = <path>
  Source = -> View [Face5,Face4,Face6,Face3,Face2]
  TreeRank = 249
FEATURE [TechDraw::DrawHatch] Hatch010  label="Hatch010F0"
  HatchPattern = <path>
  Source = -> View [Face0]
  TreeRank = 250
FEATURE [TechDraw::DrawViewDimension] Dimension043
  Arbitrary = false
  ArbitraryTolerances = false
  EqualTolerance = true
  FormatSpec = %.1f
  FormatSpecOverTolerance = %+.1f
  FormatSpecUnderTolerance = %+.1f
  Inverted = false
  LockPosition = false
  MeasureType = 1
  OverTolerance = 0
  References2D = -> [View]
  Rotation = 0
  ScaleType = 0
  TheoreticalExact = false
  TreeRank = 251
  Type = 1
  UnderTolerance = 0
  X = 60.5005
  Y = 28.1608
FEATURE [TechDraw::DrawViewDimension] Dimension044
  Arbitrary = false
  ArbitraryTolerances = false
  EqualTolerance = true
  FormatSpec = %.1f
  FormatSpecOverTolerance = %+.1f
  FormatSpecUnderTolerance = %+.1f
  Inverted = false
  LockPosition = false
  MeasureType = 1
  OverTolerance = 0
  References2D = -> [View]
  Rotation = 0
  ScaleType = 0
  TheoreticalExact = false
  TreeRank = 252
  Type = 2
  UnderTolerance = 0
  X = 63.2352
  Y = 16.0975
FEATURE [TechDraw::DrawViewBalloon] Balloon005
  BubbleShape = 3
  EndType = 0
  EndTypeScale = 1
  KinkLength = 5
  LockPosition = false
  OriginX = 19.3761
  OriginY = -14.7271
  Rotation = 0
  ScaleType = 0
  ShapeScale = 1
  SourceView = -> View
  Text = Adhesive copper tape touch pads, approx. 10 mm x 10 mm, 5 nos for UP / DOWN / LEFT / RIGHT / ENTER
  TextWrapLen = 100
  TreeRank = 253
  X = 125.811
  Y = -48.9134
FEATURE [TechDraw::DrawViewBalloon] Balloon006
  BubbleShape = 3
  EndType = 0
  EndTypeScale = 1
  KinkLength = 5
  LockPosition = false
  OriginX = 25.8615
  OriginY = -8.19221
  Rotation = 0
  ScaleType = 0
  ShapeScale = 1
  SourceView = -> View
  Text = Holes in back cover to pass through wires between ESP32 and copper pads
  TextWrapLen = 80
  TreeRank = 254
  X = 115.864
  Y = -28.3006
FEATURE [TechDraw::DrawPage] Page006
  KeepUpdated = true
  NextBalloonIndex = 3
  ProjectionType = 0
  Template = -> Template006
  TreeRank = 241
  Views = -> [View,Dimension043,Dimension044,Balloon005,Balloon006]
FEATURE [App::DocumentObjectGroup] Group001  label="Tech_Draw"
  ClaimAllChildren = true
  ExportMode = 1
  Group = -> [Page,Page001,Page002,Page003,Page004,Page005,Page006]
  TreeRank = 237
  _GroupVersion = 1
FEATURE [TechDraw::DrawSVGTemplate] Template007
  EditableTexts = AUTHOR_NAME=Anool J M; DRAWING_TITLE=Exploded view; FC-DATE=02/04/2023; FC-REV=REV A; FC-SC=1:1; FC-SH=8 / 8; FC-SI=A4; PN=Infinity_exploded
  Height = 210
  Orientation = 1
  TreeRank = 256
  Width = 297
FEATURE [TechDraw::DrawViewImage] Image
  Height = 100
  ImageFile = <userpath>/projects-git/MAKERS_ASYLUM/InfinityMirror/fabricate/PDF/infinity_exploded_view.png
  LockPosition = false
  Rotation = 0
  ScaleType = 2
  TreeRank = 259
  Width = 100
  X = 242.132
  Y = 149.575
FEATURE [TechDraw::DrawViewPart] View001
  CoarseView = false
  Direction = (1,0,0)
  Focus = 100
  HardHidden = true
  IsoCount = 0
  IsoHidden = false
  IsoVisible = false
  LockPosition = false
  Perspective = false
  Rotation = 0
  ScaleType = 0
  SeamHidden = false
  SeamVisible = false
  SmoothHidden = false
  SmoothVisible = true
  Source = -> [Body,Body012,Compound001,Body013,Body014,Body015,Body016,Body017,Screw,Screw001,Screw002,Nut,Nut001,Nut002]
  TreeRank = 260
  X = 68.0178
  XDirection = (0,1,0)
  Y = 122.589
FEATURE [TechDraw::DrawViewBalloon] Balloon007
  BubbleShape = 3
  EndType = 0
  EndTypeScale = 1
  KinkLength = 5
  LockPosition = false
  OriginX = 46.3541
  OriginY = 59.6954
  Rotation = 0
  ScaleType = 0
  ShapeScale = 1
  SourceView = -> View001
  Text = Screw, M3 x 38 mm, 3 nos
  TextWrapLen = 60
  TreeRank = 261
  X = 93.3431
  Y = 61.3429
FEATURE [TechDraw::DrawViewBalloon] Balloon008
  BubbleShape = 3
  EndType = 0
  EndTypeScale = 1
  KinkLength = 5
  LockPosition = false
  OriginX = 32.0542
  OriginY = 56.5894
  Rotation = 0
  ScaleType = 0
  ShapeScale = 1
  SourceView = -> View001
  Text = Front Bezel
  TextWrapLen = 60
  TreeRank = 262
  X = 92.3064
  Y = 48.9834
FEATURE [TechDraw::DrawViewBalloon] Balloon009
  BubbleShape = 3
  EndType = 0
  EndTypeScale = 1
  KinkLength = 5
  LockPosition = false
  OriginX = 26.9464
  OriginY = 14.1718
  Rotation = 0
  ScaleType = 0
  ShapeScale = 1
  SourceView = -> View001
  Text = Mirror, one way. Tight fit with top surface of PVC upper spacer
  TextWrapLen = 60
  TreeRank = 263
  X = 94.6461
  Y = 36.1031
FEATURE [TechDraw::DrawViewBalloon] Balloon010
  BubbleShape = 3
  EndType = 0
  EndTypeScale = 1
  KinkLength = 5
  LockPosition = false
  OriginX = 26.058
  OriginY = 3.95611
  Rotation = 0
  ScaleType = 0
  ShapeScale = 1
  SourceView = -> View001
  Text = PVC upper spacer
  TextWrapLen = 60
  TreeRank = 264
  X = 91.3043
  Y = 21.0988
FEATURE [TechDraw::DrawViewBalloon] Balloon011
  BubbleShape = 3
  EndType = 0
  EndTypeScale = 1
  KinkLength = 5
  LockPosition = false
  OriginX = 25.3918
  OriginY = -9.14668
  Rotation = 0
  ScaleType = 0
  ShapeScale = 1
  SourceView = -> View001
  Text = Main mirror, 100% reflectance
  TextWrapLen = 60
  TreeRank = 265
  X = 91.5416
  Y = 10.0745
FEATURE [TechDraw::DrawViewBalloon] Balloon012
  BubbleShape = 3
  EndType = 0
  EndTypeScale = 1
  KinkLength = 5
  LockPosition = false
  OriginX = 26.2801
  OriginY = -21.2316
  Rotation = 0
  ScaleType = 0
  ShapeScale = 1
  SourceView = -> View001
  Text = PVC lower spacer
  TextWrapLen = 60
  TreeRank = 266
  X = 90.5793
  Y = -1.12154
FEATURE [TechDraw::DrawViewBalloon] Balloon013
  BubbleShape = 3
  EndType = 0
  EndTypeScale = 1
  KinkLength = 5
  LockPosition = false
  OriginX = 10.3951
  OriginY = -40.3553
  Rotation = 0
  ScaleType = 0
  ShapeScale = 1
  SourceView = -> View001
  Text = NodeMCU ESP32
  TextWrapLen = 60
  TreeRank = 267
  X = 88.2288
  Y = -14.1863
FEATURE [TechDraw::DrawViewBalloon] Balloon014
  BubbleShape = 3
  EndType = 0
  EndTypeScale = 1
  KinkLength = 5
  LockPosition = false
  OriginX = 26.4343
  OriginY = -52.6931
  Rotation = 0
  ScaleType = 0
  ShapeScale = 1
  SourceView = -> View001
  Text = Back cover
  TextWrapLen = 60
  TreeRank = 268
  X = 87.7661
  Y = -28.2206
FEATURE [TechDraw::DrawViewBalloon] Balloon015
  BubbleShape = 3
  EndType = 0
  EndTypeScale = 1
  KinkLength = 5
  LockPosition = false
  OriginX = 45.2496
  OriginY = -61.0212
  Rotation = 0
  ScaleType = 0
  ShapeScale = 1
  SourceView = -> View001
  Text = Dome nuts, M3, 3 nos
  TextWrapLen = 60
  TreeRank = 269
  X = 87.7808
  Y = -42.5487
FEATURE [TechDraw::DrawViewBalloon] Balloon016
  BubbleShape = 3
  EndType = 0
  EndTypeScale = 1
  KinkLength = 5
  LockPosition = false
  OriginX = 18.7232
  OriginY = -59.3247
  Rotation = 0
  ScaleType = 0
  ShapeScale = 1
  SourceView = -> View001
  Text = Adhesive copper tape for touch pads
  TextWrapLen = 60
  TreeRank = 270
  X = 87.1492
  Y = -66.0053
FEATURE [TechDraw::DrawPage] Page007
  KeepUpdated = true
  NextBalloonIndex = 16
  ProjectionType = 0
  Template = -> Template007
  TreeRank = 257
  Views = -> [Image,View001,Balloon007,Balloon008,Balloon009,Balloon010,Balloon011,Balloon012,Balloon013,Balloon014,Balloon015,Balloon016]
note: 8 file-system paths scrubbed to <path> (originals preserved in the JSON sidecar)
